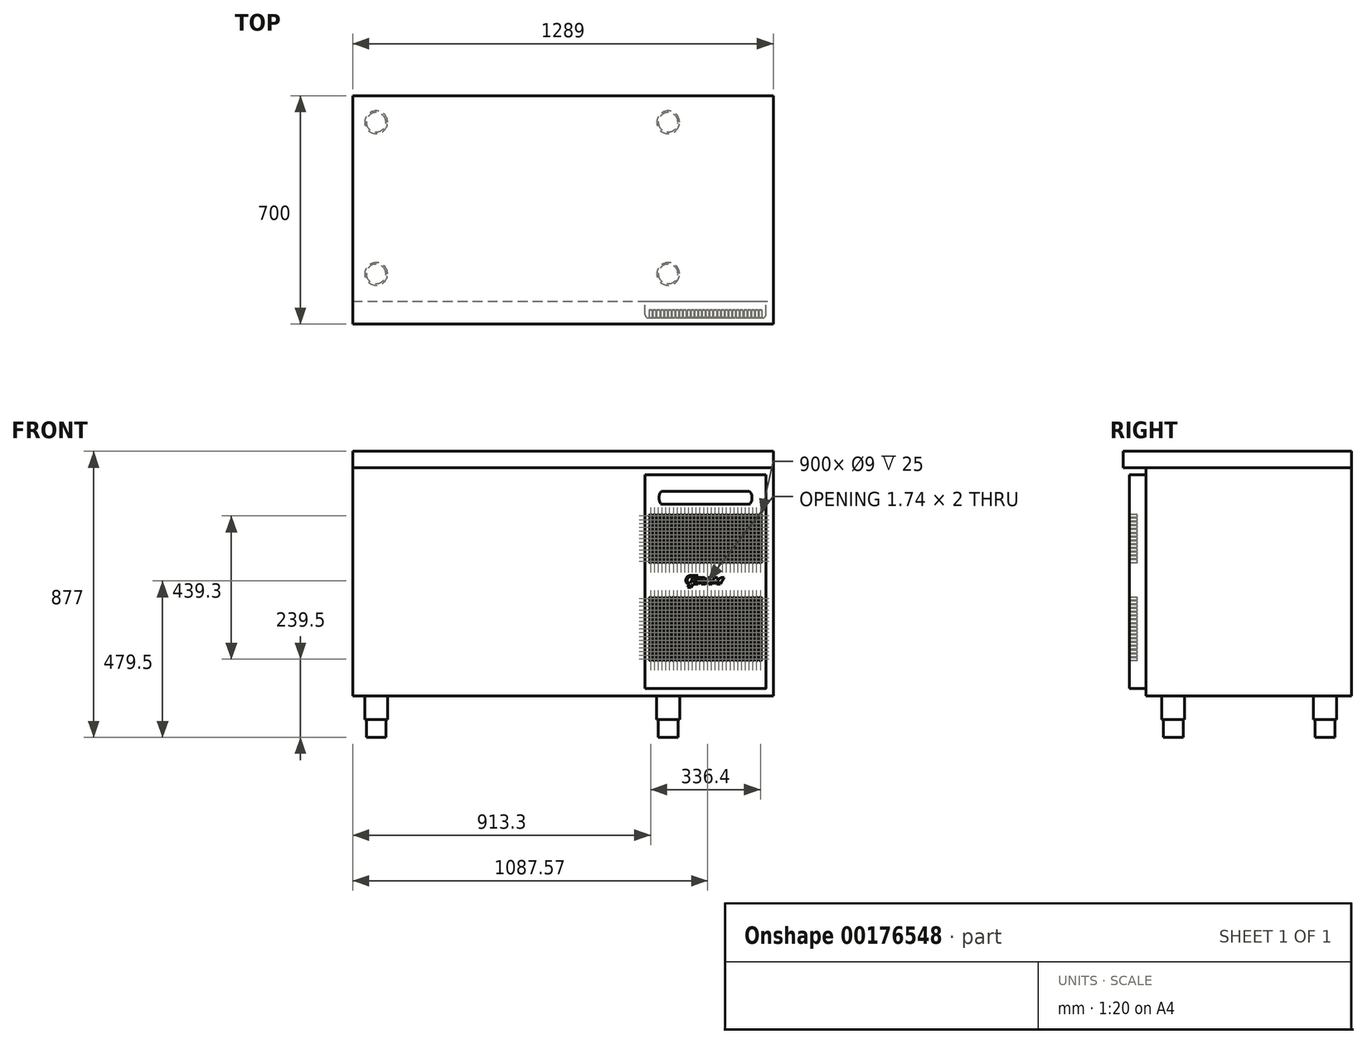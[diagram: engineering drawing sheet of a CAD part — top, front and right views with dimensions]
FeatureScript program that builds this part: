
annotation { "Feature Type Name" : "Feature", "Feature Type Description" : "" }
export const myFeature = defineFeature(function(context is Context, id is Id, definition is map)
    precondition{}
    {
        {
            var Q0;
            Q0=qCreatedBy(makeId("Top.planeOp"),FACE);
            var sketch = newSketch(context, id + "F0", { "sketchPlane" : qUnion([Q0])});
            skLineSegment(sketch, "E0.bottom", {"start": v(644.5, 350) * mm, "end": v(-644.5, 350) * mm});
            skLineSegment(sketch, "E0.top", {"start": v(644.5, -350) * mm, "end": v(-644.5, -350) * mm});
            skLineSegment(sketch, "E0.left", {"start": v(644.5, 350) * mm, "end": v(644.5, -350) * mm});
            skLineSegment(sketch, "E0.right", {"start": v(-644.5, 350) * mm, "end": v(-644.5, -350) * mm});
            skPoint(sketch, "E0.middle", {"position": v(0, 0) * mm});
            skSolve(sketch);
        }
        {
            var Q0;
            Q0 = qSketchRegion(id + "F0", true);
            extrude(context, id + "F1", {"entities" : qUnion([Q0]), "depth" : 50 * mm});
        }
        {
            var Q0;
            Q0=makeQuery(id+"F1.opExtrude","CAP_FACE",FACE,{"disambiguationData":[OSD([sQuery(id+"F0.wireOp",EDGE,"E0.bottom"),sQuery(id+"F0.wireOp",EDGE,"E0.top"),sQuery(id+"F0.wireOp",EDGE,"E0.left"),sQuery(id+"F0.wireOp",EDGE,"E0.right")])],"isStart":true});
            var sketch = newSketch(context, id + "F2", { "sketchPlane" : qUnion([Q0])});
            skLineSegment(sketch, "E1.bottom", {"start": v(-644.5, -350) * mm, "end": v(644.5, -350) * mm});
            skLineSegment(sketch, "E1.top", {"start": v(-644.5, 280) * mm, "end": v(644.5, 280) * mm});
            skLineSegment(sketch, "E1.left", {"start": v(-644.5, -350) * mm, "end": v(-644.5, 280) * mm});
            skLineSegment(sketch, "E1.right", {"start": v(644.5, -350) * mm, "end": v(644.5, 280) * mm});
            skSolve(sketch);
        }
        {
            var Q0;
            Q0 = qSketchRegion(id + "F2", true);
            extrude(context, id + "F3", {"entities" : qUnion([Q0]), "depth" : 700 * mm});
        }
        {
            var Q0;
            Q0=makeQuery(id+"F3.opExtrude","CAP_FACE",FACE,{"disambiguationData":[OSD([sQuery(id+"F2.wireOp",EDGE,"E1.bottom"),sQuery(id+"F2.wireOp",EDGE,"E1.top"),sQuery(id+"F2.wireOp",EDGE,"E1.left"),sQuery(id+"F2.wireOp",EDGE,"E1.right")])],"isStart":false});
            var sketch = newSketch(context, id + "F4", { "sketchPlane" : qUnion([Q0])});
            skCircle(sketch, "E2", {"center": v(-572.5, 196) * mm, "radius": 35 * mm});
            skCircle(sketch, "E3", {"center": v(322.5, 196) * mm, "radius": 35 * mm});
            skCircle(sketch, "E4", {"center": v(322.5, -269) * mm, "radius": 35 * mm});
            skCircle(sketch, "E5", {"center": v(-572.5, -269) * mm, "radius": 35 * mm});
            skSolve(sketch);
        }
        {
            var Q0;
            Q0 = qSketchRegion(id + "F4", true);
            extrude(context, id + "F5", {"entities" : qUnion([Q0]), "operationType" : NewBodyOperationType.ADD, "offsetDistance" : 25 * mm, "depth" : 72 * mm});
        }
        {
            var Q0;
            Q0=makeQuery(id+"F5.opExtrude","CAP_FACE",FACE,{"disambiguationData":[OSD([sQuery(id+"F4.wireOp",EDGE,"E2")])],"isStart":false});
            var sketch = newSketch(context, id + "F6", { "sketchPlane" : qUnion([Q0])});
            skCircle(sketch, "E6", {"center": v(-572.5, 196) * mm, "radius": 30 * mm});
            skCircle(sketch, "E7", {"center": v(322.5, 196) * mm, "radius": 30 * mm});
            skCircle(sketch, "E8", {"center": v(322.5, -269) * mm, "radius": 30 * mm});
            skCircle(sketch, "E9", {"center": v(-572.5, -269) * mm, "radius": 30 * mm});
            skSolve(sketch);
        }
        {
            var Q0;
            Q0 = qSketchRegion(id + "F6", true);
            extrude(context, id + "F7", {"entities" : qUnion([Q0]), "operationType" : NewBodyOperationType.ADD, "depth" : 55 * mm});
        }
        {
            var Q0;
            Q0=makeQuery(id+"F3.opExtrude","SWEPT_FACE",FACE,{"disambiguationData":[OSD([sQuery(id+"F2.wireOp",EDGE,"E1.top")])]});
            var sketch = newSketch(context, id + "F8", { "sketchPlane" : qUnion([Q0])});
            skLineSegment(sketch, "E10.bottom", {"start": v(252, -22.5) * mm, "end": v(622, -22.5) * mm});
            skLineSegment(sketch, "E10.top", {"start": v(252, -677.5) * mm, "end": v(622, -677.5) * mm});
            skLineSegment(sketch, "E10.left", {"start": v(252, -22.5) * mm, "end": v(252, -677.5) * mm});
            skLineSegment(sketch, "E10.right", {"start": v(622, -22.5) * mm, "end": v(622, -677.5) * mm});
            skSolve(sketch);
        }
        {
            var Q0;
            Q0 = qSketchRegion(id + "F8", true);
            extrude(context, id + "F9", {"entities" : qUnion([Q0]), "operationType" : NewBodyOperationType.ADD, "depth" : 51 * mm});
        }
        {
            var Q0;
            Q0=makeQuery(id+"F9.opExtrude","CAP_EDGE",EDGE,{"disambiguationData":[OSD([sQuery(id+"F8.wireOp",EDGE,"E10.left")])],"isStart":false});
            var Q1;
            Q1=makeQuery(id+"F9.opExtrude","CAP_EDGE",EDGE,{"disambiguationData":[OSD([sQuery(id+"F8.wireOp",EDGE,"E10.right")])],"isStart":false});
            fillet(context, id + "F10", {"entities" : qUnion([Q0, Q1]), "radius" : 10 * mm, "tangentPropagation" : true, "allowEdgeOverflow" : false});
        }
        {
            var Q0;
            Q0=makeQuery(id+"F9.opExtrude","CAP_FACE",FACE,{"disambiguationData":[OSD([sQuery(id+"F8.wireOp",EDGE,"E10.bottom"),sQuery(id+"F8.wireOp",EDGE,"E10.top"),sQuery(id+"F8.wireOp",EDGE,"E10.left"),sQuery(id+"F8.wireOp",EDGE,"E10.right")])],"isStart":false});
            var sketch = newSketch(context, id + "F11", { "sketchPlane" : qUnion([Q0])});
            skCircle(sketch, "E11", {"center": v(268.8, -587.5) * mm, "radius": 4.5 * mm});
            skCircle(sketch, "E12.0.1.0", {"center": v(268.8, -575.9) * mm, "radius": 4.5 * mm});
            skCircle(sketch, "E12.0.2.0", {"center": v(268.8, -564.3) * mm, "radius": 4.5 * mm});
            skCircle(sketch, "E12.0.3.0", {"center": v(268.8, -552.7) * mm, "radius": 4.5 * mm});
            skCircle(sketch, "E12.0.4.0", {"center": v(268.8, -541.1) * mm, "radius": 4.5 * mm});
            skCircle(sketch, "E12.0.5.0", {"center": v(268.8, -529.5) * mm, "radius": 4.5 * mm});
            skCircle(sketch, "E12.0.6.0", {"center": v(268.8, -517.9) * mm, "radius": 4.5 * mm});
            skCircle(sketch, "E12.0.7.0", {"center": v(268.8, -506.3) * mm, "radius": 4.5 * mm});
            skCircle(sketch, "E12.0.8.0", {"center": v(268.8, -494.7) * mm, "radius": 4.5 * mm});
            skCircle(sketch, "E12.0.9.0", {"center": v(268.8, -483.1) * mm, "radius": 4.5 * mm});
            skCircle(sketch, "E12.0.10.0", {"center": v(268.8, -471.5) * mm, "radius": 4.5 * mm});
            skCircle(sketch, "E12.0.11.0", {"center": v(268.8, -459.9) * mm, "radius": 4.5 * mm});
            skCircle(sketch, "E12.0.12.0", {"center": v(268.8, -448.3) * mm, "radius": 4.5 * mm});
            skCircle(sketch, "E12.0.13.0", {"center": v(268.8, -436.7) * mm, "radius": 4.5 * mm});
            skCircle(sketch, "E12.0.14.0", {"center": v(268.8, -425.1) * mm, "radius": 4.5 * mm});
            skCircle(sketch, "E12.0.15.0", {"center": v(268.8, -413.5) * mm, "radius": 4.5 * mm});
            skCircle(sketch, "E12.0.16.0", {"center": v(268.8, -401.9) * mm, "radius": 4.5 * mm});
            skCircle(sketch, "E12.1.0.0", {"center": v(280.4, -587.5) * mm, "radius": 4.5 * mm});
            skCircle(sketch, "E12.1.1.0", {"center": v(280.4, -575.9) * mm, "radius": 4.5 * mm});
            skCircle(sketch, "E12.1.2.0", {"center": v(280.4, -564.3) * mm, "radius": 4.5 * mm});
            skCircle(sketch, "E12.1.3.0", {"center": v(280.4, -552.7) * mm, "radius": 4.5 * mm});
            skCircle(sketch, "E12.1.4.0", {"center": v(280.4, -541.1) * mm, "radius": 4.5 * mm});
            skCircle(sketch, "E12.1.5.0", {"center": v(280.4, -529.5) * mm, "radius": 4.5 * mm});
            skCircle(sketch, "E12.1.6.0", {"center": v(280.4, -517.9) * mm, "radius": 4.5 * mm});
            skCircle(sketch, "E12.1.7.0", {"center": v(280.4, -506.3) * mm, "radius": 4.5 * mm});
            skCircle(sketch, "E12.1.8.0", {"center": v(280.4, -494.7) * mm, "radius": 4.5 * mm});
            skCircle(sketch, "E12.1.9.0", {"center": v(280.4, -483.1) * mm, "radius": 4.5 * mm});
            skCircle(sketch, "E12.1.10.0", {"center": v(280.4, -471.5) * mm, "radius": 4.5 * mm});
            skCircle(sketch, "E12.1.11.0", {"center": v(280.4, -459.9) * mm, "radius": 4.5 * mm});
            skCircle(sketch, "E12.1.12.0", {"center": v(280.4, -448.3) * mm, "radius": 4.5 * mm});
            skCircle(sketch, "E12.1.13.0", {"center": v(280.4, -436.7) * mm, "radius": 4.5 * mm});
            skCircle(sketch, "E12.1.14.0", {"center": v(280.4, -425.1) * mm, "radius": 4.5 * mm});
            skCircle(sketch, "E12.1.15.0", {"center": v(280.4, -413.5) * mm, "radius": 4.5 * mm});
            skCircle(sketch, "E12.1.16.0", {"center": v(280.4, -401.9) * mm, "radius": 4.5 * mm});
            skCircle(sketch, "E12.2.0.0", {"center": v(292, -587.5) * mm, "radius": 4.5 * mm});
            skCircle(sketch, "E12.2.1.0", {"center": v(292, -575.9) * mm, "radius": 4.5 * mm});
            skCircle(sketch, "E12.2.2.0", {"center": v(292, -564.3) * mm, "radius": 4.5 * mm});
            skCircle(sketch, "E12.2.3.0", {"center": v(292, -552.7) * mm, "radius": 4.5 * mm});
            skCircle(sketch, "E12.2.4.0", {"center": v(292, -541.1) * mm, "radius": 4.5 * mm});
            skCircle(sketch, "E12.2.5.0", {"center": v(292, -529.5) * mm, "radius": 4.5 * mm});
            skCircle(sketch, "E12.2.6.0", {"center": v(292, -517.9) * mm, "radius": 4.5 * mm});
            skCircle(sketch, "E12.2.7.0", {"center": v(292, -506.3) * mm, "radius": 4.5 * mm});
            skCircle(sketch, "E12.2.8.0", {"center": v(292, -494.7) * mm, "radius": 4.5 * mm});
            skCircle(sketch, "E12.2.9.0", {"center": v(292, -483.1) * mm, "radius": 4.5 * mm});
            skCircle(sketch, "E12.2.10.0", {"center": v(292, -471.5) * mm, "radius": 4.5 * mm});
            skCircle(sketch, "E12.2.11.0", {"center": v(292, -459.9) * mm, "radius": 4.5 * mm});
            skCircle(sketch, "E12.2.12.0", {"center": v(292, -448.3) * mm, "radius": 4.5 * mm});
            skCircle(sketch, "E12.2.13.0", {"center": v(292, -436.7) * mm, "radius": 4.5 * mm});
            skCircle(sketch, "E12.2.14.0", {"center": v(292, -425.1) * mm, "radius": 4.5 * mm});
            skCircle(sketch, "E12.2.15.0", {"center": v(292, -413.5) * mm, "radius": 4.5 * mm});
            skCircle(sketch, "E12.2.16.0", {"center": v(292, -401.9) * mm, "radius": 4.5 * mm});
            skCircle(sketch, "E12.3.0.0", {"center": v(303.6, -587.5) * mm, "radius": 4.5 * mm});
            skCircle(sketch, "E12.3.1.0", {"center": v(303.6, -575.9) * mm, "radius": 4.5 * mm});
            skCircle(sketch, "E12.3.2.0", {"center": v(303.6, -564.3) * mm, "radius": 4.5 * mm});
            skCircle(sketch, "E12.3.3.0", {"center": v(303.6, -552.7) * mm, "radius": 4.5 * mm});
            skCircle(sketch, "E12.3.4.0", {"center": v(303.6, -541.1) * mm, "radius": 4.5 * mm});
            skCircle(sketch, "E12.3.5.0", {"center": v(303.6, -529.5) * mm, "radius": 4.5 * mm});
            skCircle(sketch, "E12.3.6.0", {"center": v(303.6, -517.9) * mm, "radius": 4.5 * mm});
            skCircle(sketch, "E12.3.7.0", {"center": v(303.6, -506.3) * mm, "radius": 4.5 * mm});
            skCircle(sketch, "E12.3.8.0", {"center": v(303.6, -494.7) * mm, "radius": 4.5 * mm});
            skCircle(sketch, "E12.3.9.0", {"center": v(303.6, -483.1) * mm, "radius": 4.5 * mm});
            skCircle(sketch, "E12.3.10.0", {"center": v(303.6, -471.5) * mm, "radius": 4.5 * mm});
            skCircle(sketch, "E12.3.11.0", {"center": v(303.6, -459.9) * mm, "radius": 4.5 * mm});
            skCircle(sketch, "E12.3.12.0", {"center": v(303.6, -448.3) * mm, "radius": 4.5 * mm});
            skCircle(sketch, "E12.3.13.0", {"center": v(303.6, -436.7) * mm, "radius": 4.5 * mm});
            skCircle(sketch, "E12.3.14.0", {"center": v(303.6, -425.1) * mm, "radius": 4.5 * mm});
            skCircle(sketch, "E12.3.15.0", {"center": v(303.6, -413.5) * mm, "radius": 4.5 * mm});
            skCircle(sketch, "E12.3.16.0", {"center": v(303.6, -401.9) * mm, "radius": 4.5 * mm});
            skCircle(sketch, "E12.4.0.0", {"center": v(315.2, -587.5) * mm, "radius": 4.5 * mm});
            skCircle(sketch, "E12.4.1.0", {"center": v(315.2, -575.9) * mm, "radius": 4.5 * mm});
            skCircle(sketch, "E12.4.2.0", {"center": v(315.2, -564.3) * mm, "radius": 4.5 * mm});
            skCircle(sketch, "E12.4.3.0", {"center": v(315.2, -552.7) * mm, "radius": 4.5 * mm});
            skCircle(sketch, "E12.4.4.0", {"center": v(315.2, -541.1) * mm, "radius": 4.5 * mm});
            skCircle(sketch, "E12.4.5.0", {"center": v(315.2, -529.5) * mm, "radius": 4.5 * mm});
            skCircle(sketch, "E12.4.6.0", {"center": v(315.2, -517.9) * mm, "radius": 4.5 * mm});
            skCircle(sketch, "E12.4.7.0", {"center": v(315.2, -506.3) * mm, "radius": 4.5 * mm});
            skCircle(sketch, "E12.4.8.0", {"center": v(315.2, -494.7) * mm, "radius": 4.5 * mm});
            skCircle(sketch, "E12.4.9.0", {"center": v(315.2, -483.1) * mm, "radius": 4.5 * mm});
            skCircle(sketch, "E12.4.10.0", {"center": v(315.2, -471.5) * mm, "radius": 4.5 * mm});
            skCircle(sketch, "E12.4.11.0", {"center": v(315.2, -459.9) * mm, "radius": 4.5 * mm});
            skCircle(sketch, "E12.4.12.0", {"center": v(315.2, -448.3) * mm, "radius": 4.5 * mm});
            skCircle(sketch, "E12.4.13.0", {"center": v(315.2, -436.7) * mm, "radius": 4.5 * mm});
            skCircle(sketch, "E12.4.14.0", {"center": v(315.2, -425.1) * mm, "radius": 4.5 * mm});
            skCircle(sketch, "E12.4.15.0", {"center": v(315.2, -413.5) * mm, "radius": 4.5 * mm});
            skCircle(sketch, "E12.4.16.0", {"center": v(315.2, -401.9) * mm, "radius": 4.5 * mm});
            skCircle(sketch, "E12.5.0.0", {"center": v(326.8, -587.5) * mm, "radius": 4.5 * mm});
            skCircle(sketch, "E12.5.1.0", {"center": v(326.8, -575.9) * mm, "radius": 4.5 * mm});
            skCircle(sketch, "E12.5.2.0", {"center": v(326.8, -564.3) * mm, "radius": 4.5 * mm});
            skCircle(sketch, "E12.5.3.0", {"center": v(326.8, -552.7) * mm, "radius": 4.5 * mm});
            skCircle(sketch, "E12.5.4.0", {"center": v(326.8, -541.1) * mm, "radius": 4.5 * mm});
            skCircle(sketch, "E12.5.5.0", {"center": v(326.8, -529.5) * mm, "radius": 4.5 * mm});
            skCircle(sketch, "E12.5.6.0", {"center": v(326.8, -517.9) * mm, "radius": 4.5 * mm});
            skCircle(sketch, "E12.5.7.0", {"center": v(326.8, -506.3) * mm, "radius": 4.5 * mm});
            skCircle(sketch, "E12.5.8.0", {"center": v(326.8, -494.7) * mm, "radius": 4.5 * mm});
            skCircle(sketch, "E12.5.9.0", {"center": v(326.8, -483.1) * mm, "radius": 4.5 * mm});
            skCircle(sketch, "E12.5.10.0", {"center": v(326.8, -471.5) * mm, "radius": 4.5 * mm});
            skCircle(sketch, "E12.5.11.0", {"center": v(326.8, -459.9) * mm, "radius": 4.5 * mm});
            skCircle(sketch, "E12.5.12.0", {"center": v(326.8, -448.3) * mm, "radius": 4.5 * mm});
            skCircle(sketch, "E12.5.13.0", {"center": v(326.8, -436.7) * mm, "radius": 4.5 * mm});
            skCircle(sketch, "E12.5.14.0", {"center": v(326.8, -425.1) * mm, "radius": 4.5 * mm});
            skCircle(sketch, "E12.5.15.0", {"center": v(326.8, -413.5) * mm, "radius": 4.5 * mm});
            skCircle(sketch, "E12.5.16.0", {"center": v(326.8, -401.9) * mm, "radius": 4.5 * mm});
            skCircle(sketch, "E12.6.0.0", {"center": v(338.4, -587.5) * mm, "radius": 4.5 * mm});
            skCircle(sketch, "E12.6.1.0", {"center": v(338.4, -575.9) * mm, "radius": 4.5 * mm});
            skCircle(sketch, "E12.6.2.0", {"center": v(338.4, -564.3) * mm, "radius": 4.5 * mm});
            skCircle(sketch, "E12.6.3.0", {"center": v(338.4, -552.7) * mm, "radius": 4.5 * mm});
            skCircle(sketch, "E12.6.4.0", {"center": v(338.4, -541.1) * mm, "radius": 4.5 * mm});
            skCircle(sketch, "E12.6.5.0", {"center": v(338.4, -529.5) * mm, "radius": 4.5 * mm});
            skCircle(sketch, "E12.6.6.0", {"center": v(338.4, -517.9) * mm, "radius": 4.5 * mm});
            skCircle(sketch, "E12.6.7.0", {"center": v(338.4, -506.3) * mm, "radius": 4.5 * mm});
            skCircle(sketch, "E12.6.8.0", {"center": v(338.4, -494.7) * mm, "radius": 4.5 * mm});
            skCircle(sketch, "E12.6.9.0", {"center": v(338.4, -483.1) * mm, "radius": 4.5 * mm});
            skCircle(sketch, "E12.6.10.0", {"center": v(338.4, -471.5) * mm, "radius": 4.5 * mm});
            skCircle(sketch, "E12.6.11.0", {"center": v(338.4, -459.9) * mm, "radius": 4.5 * mm});
            skCircle(sketch, "E12.6.12.0", {"center": v(338.4, -448.3) * mm, "radius": 4.5 * mm});
            skCircle(sketch, "E12.6.13.0", {"center": v(338.4, -436.7) * mm, "radius": 4.5 * mm});
            skCircle(sketch, "E12.6.14.0", {"center": v(338.4, -425.1) * mm, "radius": 4.5 * mm});
            skCircle(sketch, "E12.6.15.0", {"center": v(338.4, -413.5) * mm, "radius": 4.5 * mm});
            skCircle(sketch, "E12.6.16.0", {"center": v(338.4, -401.9) * mm, "radius": 4.5 * mm});
            skCircle(sketch, "E12.7.0.0", {"center": v(350, -587.5) * mm, "radius": 4.5 * mm});
            skCircle(sketch, "E12.7.1.0", {"center": v(350, -575.9) * mm, "radius": 4.5 * mm});
            skCircle(sketch, "E12.7.2.0", {"center": v(350, -564.3) * mm, "radius": 4.5 * mm});
            skCircle(sketch, "E12.7.3.0", {"center": v(350, -552.7) * mm, "radius": 4.5 * mm});
            skCircle(sketch, "E12.7.4.0", {"center": v(350, -541.1) * mm, "radius": 4.5 * mm});
            skCircle(sketch, "E12.7.5.0", {"center": v(350, -529.5) * mm, "radius": 4.5 * mm});
            skCircle(sketch, "E12.7.6.0", {"center": v(350, -517.9) * mm, "radius": 4.5 * mm});
            skCircle(sketch, "E12.7.7.0", {"center": v(350, -506.3) * mm, "radius": 4.5 * mm});
            skCircle(sketch, "E12.7.8.0", {"center": v(350, -494.7) * mm, "radius": 4.5 * mm});
            skCircle(sketch, "E12.7.9.0", {"center": v(350, -483.1) * mm, "radius": 4.5 * mm});
            skCircle(sketch, "E12.7.10.0", {"center": v(350, -471.5) * mm, "radius": 4.5 * mm});
            skCircle(sketch, "E12.7.11.0", {"center": v(350, -459.9) * mm, "radius": 4.5 * mm});
            skCircle(sketch, "E12.7.12.0", {"center": v(350, -448.3) * mm, "radius": 4.5 * mm});
            skCircle(sketch, "E12.7.13.0", {"center": v(350, -436.7) * mm, "radius": 4.5 * mm});
            skCircle(sketch, "E12.7.14.0", {"center": v(350, -425.1) * mm, "radius": 4.5 * mm});
            skCircle(sketch, "E12.7.15.0", {"center": v(350, -413.5) * mm, "radius": 4.5 * mm});
            skCircle(sketch, "E12.7.16.0", {"center": v(350, -401.9) * mm, "radius": 4.5 * mm});
            skCircle(sketch, "E12.8.0.0", {"center": v(361.6, -587.5) * mm, "radius": 4.5 * mm});
            skCircle(sketch, "E12.8.1.0", {"center": v(361.6, -575.9) * mm, "radius": 4.5 * mm});
            skCircle(sketch, "E12.8.2.0", {"center": v(361.6, -564.3) * mm, "radius": 4.5 * mm});
            skCircle(sketch, "E12.8.3.0", {"center": v(361.6, -552.7) * mm, "radius": 4.5 * mm});
            skCircle(sketch, "E12.8.4.0", {"center": v(361.6, -541.1) * mm, "radius": 4.5 * mm});
            skCircle(sketch, "E12.8.5.0", {"center": v(361.6, -529.5) * mm, "radius": 4.5 * mm});
            skCircle(sketch, "E12.8.6.0", {"center": v(361.6, -517.9) * mm, "radius": 4.5 * mm});
            skCircle(sketch, "E12.8.7.0", {"center": v(361.6, -506.3) * mm, "radius": 4.5 * mm});
            skCircle(sketch, "E12.8.8.0", {"center": v(361.6, -494.7) * mm, "radius": 4.5 * mm});
            skCircle(sketch, "E12.8.9.0", {"center": v(361.6, -483.1) * mm, "radius": 4.5 * mm});
            skCircle(sketch, "E12.8.10.0", {"center": v(361.6, -471.5) * mm, "radius": 4.5 * mm});
            skCircle(sketch, "E12.8.11.0", {"center": v(361.6, -459.9) * mm, "radius": 4.5 * mm});
            skCircle(sketch, "E12.8.12.0", {"center": v(361.6, -448.3) * mm, "radius": 4.5 * mm});
            skCircle(sketch, "E12.8.13.0", {"center": v(361.6, -436.7) * mm, "radius": 4.5 * mm});
            skCircle(sketch, "E12.8.14.0", {"center": v(361.6, -425.1) * mm, "radius": 4.5 * mm});
            skCircle(sketch, "E12.8.15.0", {"center": v(361.6, -413.5) * mm, "radius": 4.5 * mm});
            skCircle(sketch, "E12.8.16.0", {"center": v(361.6, -401.9) * mm, "radius": 4.5 * mm});
            skCircle(sketch, "E12.9.0.0", {"center": v(373.2, -587.5) * mm, "radius": 4.5 * mm});
            skCircle(sketch, "E12.9.1.0", {"center": v(373.2, -575.9) * mm, "radius": 4.5 * mm});
            skCircle(sketch, "E12.9.2.0", {"center": v(373.2, -564.3) * mm, "radius": 4.5 * mm});
            skCircle(sketch, "E12.9.3.0", {"center": v(373.2, -552.7) * mm, "radius": 4.5 * mm});
            skCircle(sketch, "E12.9.4.0", {"center": v(373.2, -541.1) * mm, "radius": 4.5 * mm});
            skCircle(sketch, "E12.9.5.0", {"center": v(373.2, -529.5) * mm, "radius": 4.5 * mm});
            skCircle(sketch, "E12.9.6.0", {"center": v(373.2, -517.9) * mm, "radius": 4.5 * mm});
            skCircle(sketch, "E12.9.7.0", {"center": v(373.2, -506.3) * mm, "radius": 4.5 * mm});
            skCircle(sketch, "E12.9.8.0", {"center": v(373.2, -494.7) * mm, "radius": 4.5 * mm});
            skCircle(sketch, "E12.9.9.0", {"center": v(373.2, -483.1) * mm, "radius": 4.5 * mm});
            skCircle(sketch, "E12.9.10.0", {"center": v(373.2, -471.5) * mm, "radius": 4.5 * mm});
            skCircle(sketch, "E12.9.11.0", {"center": v(373.2, -459.9) * mm, "radius": 4.5 * mm});
            skCircle(sketch, "E12.9.12.0", {"center": v(373.2, -448.3) * mm, "radius": 4.5 * mm});
            skCircle(sketch, "E12.9.13.0", {"center": v(373.2, -436.7) * mm, "radius": 4.5 * mm});
            skCircle(sketch, "E12.9.14.0", {"center": v(373.2, -425.1) * mm, "radius": 4.5 * mm});
            skCircle(sketch, "E12.9.15.0", {"center": v(373.2, -413.5) * mm, "radius": 4.5 * mm});
            skCircle(sketch, "E12.9.16.0", {"center": v(373.2, -401.9) * mm, "radius": 4.5 * mm});
            skCircle(sketch, "E12.10.0.0", {"center": v(384.8, -587.5) * mm, "radius": 4.5 * mm});
            skCircle(sketch, "E12.10.1.0", {"center": v(384.8, -575.9) * mm, "radius": 4.5 * mm});
            skCircle(sketch, "E12.10.2.0", {"center": v(384.8, -564.3) * mm, "radius": 4.5 * mm});
            skCircle(sketch, "E12.10.3.0", {"center": v(384.8, -552.7) * mm, "radius": 4.5 * mm});
            skCircle(sketch, "E12.10.4.0", {"center": v(384.8, -541.1) * mm, "radius": 4.5 * mm});
            skCircle(sketch, "E12.10.5.0", {"center": v(384.8, -529.5) * mm, "radius": 4.5 * mm});
            skCircle(sketch, "E12.10.6.0", {"center": v(384.8, -517.9) * mm, "radius": 4.5 * mm});
            skCircle(sketch, "E12.10.7.0", {"center": v(384.8, -506.3) * mm, "radius": 4.5 * mm});
            skCircle(sketch, "E12.10.8.0", {"center": v(384.8, -494.7) * mm, "radius": 4.5 * mm});
            skCircle(sketch, "E12.10.9.0", {"center": v(384.8, -483.1) * mm, "radius": 4.5 * mm});
            skCircle(sketch, "E12.10.10.0", {"center": v(384.8, -471.5) * mm, "radius": 4.5 * mm});
            skCircle(sketch, "E12.10.11.0", {"center": v(384.8, -459.9) * mm, "radius": 4.5 * mm});
            skCircle(sketch, "E12.10.12.0", {"center": v(384.8, -448.3) * mm, "radius": 4.5 * mm});
            skCircle(sketch, "E12.10.13.0", {"center": v(384.8, -436.7) * mm, "radius": 4.5 * mm});
            skCircle(sketch, "E12.10.14.0", {"center": v(384.8, -425.1) * mm, "radius": 4.5 * mm});
            skCircle(sketch, "E12.10.15.0", {"center": v(384.8, -413.5) * mm, "radius": 4.5 * mm});
            skCircle(sketch, "E12.10.16.0", {"center": v(384.8, -401.9) * mm, "radius": 4.5 * mm});
            skCircle(sketch, "E12.11.0.0", {"center": v(396.4, -587.5) * mm, "radius": 4.5 * mm});
            skCircle(sketch, "E12.11.1.0", {"center": v(396.4, -575.9) * mm, "radius": 4.5 * mm});
            skCircle(sketch, "E12.11.2.0", {"center": v(396.4, -564.3) * mm, "radius": 4.5 * mm});
            skCircle(sketch, "E12.11.3.0", {"center": v(396.4, -552.7) * mm, "radius": 4.5 * mm});
            skCircle(sketch, "E12.11.4.0", {"center": v(396.4, -541.1) * mm, "radius": 4.5 * mm});
            skCircle(sketch, "E12.11.5.0", {"center": v(396.4, -529.5) * mm, "radius": 4.5 * mm});
            skCircle(sketch, "E12.11.6.0", {"center": v(396.4, -517.9) * mm, "radius": 4.5 * mm});
            skCircle(sketch, "E12.11.7.0", {"center": v(396.4, -506.3) * mm, "radius": 4.5 * mm});
            skCircle(sketch, "E12.11.8.0", {"center": v(396.4, -494.7) * mm, "radius": 4.5 * mm});
            skCircle(sketch, "E12.11.9.0", {"center": v(396.4, -483.1) * mm, "radius": 4.5 * mm});
            skCircle(sketch, "E12.11.10.0", {"center": v(396.4, -471.5) * mm, "radius": 4.5 * mm});
            skCircle(sketch, "E12.11.11.0", {"center": v(396.4, -459.9) * mm, "radius": 4.5 * mm});
            skCircle(sketch, "E12.11.12.0", {"center": v(396.4, -448.3) * mm, "radius": 4.5 * mm});
            skCircle(sketch, "E12.11.13.0", {"center": v(396.4, -436.7) * mm, "radius": 4.5 * mm});
            skCircle(sketch, "E12.11.14.0", {"center": v(396.4, -425.1) * mm, "radius": 4.5 * mm});
            skCircle(sketch, "E12.11.15.0", {"center": v(396.4, -413.5) * mm, "radius": 4.5 * mm});
            skCircle(sketch, "E12.11.16.0", {"center": v(396.4, -401.9) * mm, "radius": 4.5 * mm});
            skCircle(sketch, "E12.12.0.0", {"center": v(408, -587.5) * mm, "radius": 4.5 * mm});
            skCircle(sketch, "E12.12.1.0", {"center": v(408, -575.9) * mm, "radius": 4.5 * mm});
            skCircle(sketch, "E12.12.2.0", {"center": v(408, -564.3) * mm, "radius": 4.5 * mm});
            skCircle(sketch, "E12.12.3.0", {"center": v(408, -552.7) * mm, "radius": 4.5 * mm});
            skCircle(sketch, "E12.12.4.0", {"center": v(408, -541.1) * mm, "radius": 4.5 * mm});
            skCircle(sketch, "E12.12.5.0", {"center": v(408, -529.5) * mm, "radius": 4.5 * mm});
            skCircle(sketch, "E12.12.6.0", {"center": v(408, -517.9) * mm, "radius": 4.5 * mm});
            skCircle(sketch, "E12.12.7.0", {"center": v(408, -506.3) * mm, "radius": 4.5 * mm});
            skCircle(sketch, "E12.12.8.0", {"center": v(408, -494.7) * mm, "radius": 4.5 * mm});
            skCircle(sketch, "E12.12.9.0", {"center": v(408, -483.1) * mm, "radius": 4.5 * mm});
            skCircle(sketch, "E12.12.10.0", {"center": v(408, -471.5) * mm, "radius": 4.5 * mm});
            skCircle(sketch, "E12.12.11.0", {"center": v(408, -459.9) * mm, "radius": 4.5 * mm});
            skCircle(sketch, "E12.12.12.0", {"center": v(408, -448.3) * mm, "radius": 4.5 * mm});
            skCircle(sketch, "E12.12.13.0", {"center": v(408, -436.7) * mm, "radius": 4.5 * mm});
            skCircle(sketch, "E12.12.14.0", {"center": v(408, -425.1) * mm, "radius": 4.5 * mm});
            skCircle(sketch, "E12.12.15.0", {"center": v(408, -413.5) * mm, "radius": 4.5 * mm});
            skCircle(sketch, "E12.12.16.0", {"center": v(408, -401.9) * mm, "radius": 4.5 * mm});
            skCircle(sketch, "E12.13.0.0", {"center": v(419.6, -587.5) * mm, "radius": 4.5 * mm});
            skCircle(sketch, "E12.13.1.0", {"center": v(419.6, -575.9) * mm, "radius": 4.5 * mm});
            skCircle(sketch, "E12.13.2.0", {"center": v(419.6, -564.3) * mm, "radius": 4.5 * mm});
            skCircle(sketch, "E12.13.3.0", {"center": v(419.6, -552.7) * mm, "radius": 4.5 * mm});
            skCircle(sketch, "E12.13.4.0", {"center": v(419.6, -541.1) * mm, "radius": 4.5 * mm});
            skCircle(sketch, "E12.13.5.0", {"center": v(419.6, -529.5) * mm, "radius": 4.5 * mm});
            skCircle(sketch, "E12.13.6.0", {"center": v(419.6, -517.9) * mm, "radius": 4.5 * mm});
            skCircle(sketch, "E12.13.7.0", {"center": v(419.6, -506.3) * mm, "radius": 4.5 * mm});
            skCircle(sketch, "E12.13.8.0", {"center": v(419.6, -494.7) * mm, "radius": 4.5 * mm});
            skCircle(sketch, "E12.13.9.0", {"center": v(419.6, -483.1) * mm, "radius": 4.5 * mm});
            skCircle(sketch, "E12.13.10.0", {"center": v(419.6, -471.5) * mm, "radius": 4.5 * mm});
            skCircle(sketch, "E12.13.11.0", {"center": v(419.6, -459.9) * mm, "radius": 4.5 * mm});
            skCircle(sketch, "E12.13.12.0", {"center": v(419.6, -448.3) * mm, "radius": 4.5 * mm});
            skCircle(sketch, "E12.13.13.0", {"center": v(419.6, -436.7) * mm, "radius": 4.5 * mm});
            skCircle(sketch, "E12.13.14.0", {"center": v(419.6, -425.1) * mm, "radius": 4.5 * mm});
            skCircle(sketch, "E12.13.15.0", {"center": v(419.6, -413.5) * mm, "radius": 4.5 * mm});
            skCircle(sketch, "E12.13.16.0", {"center": v(419.6, -401.9) * mm, "radius": 4.5 * mm});
            skCircle(sketch, "E12.14.0.0", {"center": v(431.2, -587.5) * mm, "radius": 4.5 * mm});
            skCircle(sketch, "E12.14.1.0", {"center": v(431.2, -575.9) * mm, "radius": 4.5 * mm});
            skCircle(sketch, "E12.14.2.0", {"center": v(431.2, -564.3) * mm, "radius": 4.5 * mm});
            skCircle(sketch, "E12.14.3.0", {"center": v(431.2, -552.7) * mm, "radius": 4.5 * mm});
            skCircle(sketch, "E12.14.4.0", {"center": v(431.2, -541.1) * mm, "radius": 4.5 * mm});
            skCircle(sketch, "E12.14.5.0", {"center": v(431.2, -529.5) * mm, "radius": 4.5 * mm});
            skCircle(sketch, "E12.14.6.0", {"center": v(431.2, -517.9) * mm, "radius": 4.5 * mm});
            skCircle(sketch, "E12.14.7.0", {"center": v(431.2, -506.3) * mm, "radius": 4.5 * mm});
            skCircle(sketch, "E12.14.8.0", {"center": v(431.2, -494.7) * mm, "radius": 4.5 * mm});
            skCircle(sketch, "E12.14.9.0", {"center": v(431.2, -483.1) * mm, "radius": 4.5 * mm});
            skCircle(sketch, "E12.14.10.0", {"center": v(431.2, -471.5) * mm, "radius": 4.5 * mm});
            skCircle(sketch, "E12.14.11.0", {"center": v(431.2, -459.9) * mm, "radius": 4.5 * mm});
            skCircle(sketch, "E12.14.12.0", {"center": v(431.2, -448.3) * mm, "radius": 4.5 * mm});
            skCircle(sketch, "E12.14.13.0", {"center": v(431.2, -436.7) * mm, "radius": 4.5 * mm});
            skCircle(sketch, "E12.14.14.0", {"center": v(431.2, -425.1) * mm, "radius": 4.5 * mm});
            skCircle(sketch, "E12.14.15.0", {"center": v(431.2, -413.5) * mm, "radius": 4.5 * mm});
            skCircle(sketch, "E12.14.16.0", {"center": v(431.2, -401.9) * mm, "radius": 4.5 * mm});
            skCircle(sketch, "E12.15.0.0", {"center": v(442.8, -587.5) * mm, "radius": 4.5 * mm});
            skCircle(sketch, "E12.15.1.0", {"center": v(442.8, -575.9) * mm, "radius": 4.5 * mm});
            skCircle(sketch, "E12.15.2.0", {"center": v(442.8, -564.3) * mm, "radius": 4.5 * mm});
            skCircle(sketch, "E12.15.3.0", {"center": v(442.8, -552.7) * mm, "radius": 4.5 * mm});
            skCircle(sketch, "E12.15.4.0", {"center": v(442.8, -541.1) * mm, "radius": 4.5 * mm});
            skCircle(sketch, "E12.15.5.0", {"center": v(442.8, -529.5) * mm, "radius": 4.5 * mm});
            skCircle(sketch, "E12.15.6.0", {"center": v(442.8, -517.9) * mm, "radius": 4.5 * mm});
            skCircle(sketch, "E12.15.7.0", {"center": v(442.8, -506.3) * mm, "radius": 4.5 * mm});
            skCircle(sketch, "E12.15.8.0", {"center": v(442.8, -494.7) * mm, "radius": 4.5 * mm});
            skCircle(sketch, "E12.15.9.0", {"center": v(442.8, -483.1) * mm, "radius": 4.5 * mm});
            skCircle(sketch, "E12.15.10.0", {"center": v(442.8, -471.5) * mm, "radius": 4.5 * mm});
            skCircle(sketch, "E12.15.11.0", {"center": v(442.8, -459.9) * mm, "radius": 4.5 * mm});
            skCircle(sketch, "E12.15.12.0", {"center": v(442.8, -448.3) * mm, "radius": 4.5 * mm});
            skCircle(sketch, "E12.15.13.0", {"center": v(442.8, -436.7) * mm, "radius": 4.5 * mm});
            skCircle(sketch, "E12.15.14.0", {"center": v(442.8, -425.1) * mm, "radius": 4.5 * mm});
            skCircle(sketch, "E12.15.15.0", {"center": v(442.8, -413.5) * mm, "radius": 4.5 * mm});
            skCircle(sketch, "E12.15.16.0", {"center": v(442.8, -401.9) * mm, "radius": 4.5 * mm});
            skCircle(sketch, "E12.16.0.0", {"center": v(454.4, -587.5) * mm, "radius": 4.5 * mm});
            skCircle(sketch, "E12.16.1.0", {"center": v(454.4, -575.9) * mm, "radius": 4.5 * mm});
            skCircle(sketch, "E12.16.2.0", {"center": v(454.4, -564.3) * mm, "radius": 4.5 * mm});
            skCircle(sketch, "E12.16.3.0", {"center": v(454.4, -552.7) * mm, "radius": 4.5 * mm});
            skCircle(sketch, "E12.16.4.0", {"center": v(454.4, -541.1) * mm, "radius": 4.5 * mm});
            skCircle(sketch, "E12.16.5.0", {"center": v(454.4, -529.5) * mm, "radius": 4.5 * mm});
            skCircle(sketch, "E12.16.6.0", {"center": v(454.4, -517.9) * mm, "radius": 4.5 * mm});
            skCircle(sketch, "E12.16.7.0", {"center": v(454.4, -506.3) * mm, "radius": 4.5 * mm});
            skCircle(sketch, "E12.16.8.0", {"center": v(454.4, -494.7) * mm, "radius": 4.5 * mm});
            skCircle(sketch, "E12.16.9.0", {"center": v(454.4, -483.1) * mm, "radius": 4.5 * mm});
            skCircle(sketch, "E12.16.10.0", {"center": v(454.4, -471.5) * mm, "radius": 4.5 * mm});
            skCircle(sketch, "E12.16.11.0", {"center": v(454.4, -459.9) * mm, "radius": 4.5 * mm});
            skCircle(sketch, "E12.16.12.0", {"center": v(454.4, -448.3) * mm, "radius": 4.5 * mm});
            skCircle(sketch, "E12.16.13.0", {"center": v(454.4, -436.7) * mm, "radius": 4.5 * mm});
            skCircle(sketch, "E12.16.14.0", {"center": v(454.4, -425.1) * mm, "radius": 4.5 * mm});
            skCircle(sketch, "E12.16.15.0", {"center": v(454.4, -413.5) * mm, "radius": 4.5 * mm});
            skCircle(sketch, "E12.16.16.0", {"center": v(454.4, -401.9) * mm, "radius": 4.5 * mm});
            skCircle(sketch, "E12.17.0.0", {"center": v(466, -587.5) * mm, "radius": 4.5 * mm});
            skCircle(sketch, "E12.17.1.0", {"center": v(466, -575.9) * mm, "radius": 4.5 * mm});
            skCircle(sketch, "E12.17.2.0", {"center": v(466, -564.3) * mm, "radius": 4.5 * mm});
            skCircle(sketch, "E12.17.3.0", {"center": v(466, -552.7) * mm, "radius": 4.5 * mm});
            skCircle(sketch, "E12.17.4.0", {"center": v(466, -541.1) * mm, "radius": 4.5 * mm});
            skCircle(sketch, "E12.17.5.0", {"center": v(466, -529.5) * mm, "radius": 4.5 * mm});
            skCircle(sketch, "E12.17.6.0", {"center": v(466, -517.9) * mm, "radius": 4.5 * mm});
            skCircle(sketch, "E12.17.7.0", {"center": v(466, -506.3) * mm, "radius": 4.5 * mm});
            skCircle(sketch, "E12.17.8.0", {"center": v(466, -494.7) * mm, "radius": 4.5 * mm});
            skCircle(sketch, "E12.17.9.0", {"center": v(466, -483.1) * mm, "radius": 4.5 * mm});
            skCircle(sketch, "E12.17.10.0", {"center": v(466, -471.5) * mm, "radius": 4.5 * mm});
            skCircle(sketch, "E12.17.11.0", {"center": v(466, -459.9) * mm, "radius": 4.5 * mm});
            skCircle(sketch, "E12.17.12.0", {"center": v(466, -448.3) * mm, "radius": 4.5 * mm});
            skCircle(sketch, "E12.17.13.0", {"center": v(466, -436.7) * mm, "radius": 4.5 * mm});
            skCircle(sketch, "E12.17.14.0", {"center": v(466, -425.1) * mm, "radius": 4.5 * mm});
            skCircle(sketch, "E12.17.15.0", {"center": v(466, -413.5) * mm, "radius": 4.5 * mm});
            skCircle(sketch, "E12.17.16.0", {"center": v(466, -401.9) * mm, "radius": 4.5 * mm});
            skCircle(sketch, "E12.18.0.0", {"center": v(477.6, -587.5) * mm, "radius": 4.5 * mm});
            skCircle(sketch, "E12.18.1.0", {"center": v(477.6, -575.9) * mm, "radius": 4.5 * mm});
            skCircle(sketch, "E12.18.2.0", {"center": v(477.6, -564.3) * mm, "radius": 4.5 * mm});
            skCircle(sketch, "E12.18.3.0", {"center": v(477.6, -552.7) * mm, "radius": 4.5 * mm});
            skCircle(sketch, "E12.18.4.0", {"center": v(477.6, -541.1) * mm, "radius": 4.5 * mm});
            skCircle(sketch, "E12.18.5.0", {"center": v(477.6, -529.5) * mm, "radius": 4.5 * mm});
            skCircle(sketch, "E12.18.6.0", {"center": v(477.6, -517.9) * mm, "radius": 4.5 * mm});
            skCircle(sketch, "E12.18.7.0", {"center": v(477.6, -506.3) * mm, "radius": 4.5 * mm});
            skCircle(sketch, "E12.18.8.0", {"center": v(477.6, -494.7) * mm, "radius": 4.5 * mm});
            skCircle(sketch, "E12.18.9.0", {"center": v(477.6, -483.1) * mm, "radius": 4.5 * mm});
            skCircle(sketch, "E12.18.10.0", {"center": v(477.6, -471.5) * mm, "radius": 4.5 * mm});
            skCircle(sketch, "E12.18.11.0", {"center": v(477.6, -459.9) * mm, "radius": 4.5 * mm});
            skCircle(sketch, "E12.18.12.0", {"center": v(477.6, -448.3) * mm, "radius": 4.5 * mm});
            skCircle(sketch, "E12.18.13.0", {"center": v(477.6, -436.7) * mm, "radius": 4.5 * mm});
            skCircle(sketch, "E12.18.14.0", {"center": v(477.6, -425.1) * mm, "radius": 4.5 * mm});
            skCircle(sketch, "E12.18.15.0", {"center": v(477.6, -413.5) * mm, "radius": 4.5 * mm});
            skCircle(sketch, "E12.18.16.0", {"center": v(477.6, -401.9) * mm, "radius": 4.5 * mm});
            skCircle(sketch, "E12.19.0.0", {"center": v(489.2, -587.5) * mm, "radius": 4.5 * mm});
            skCircle(sketch, "E12.19.1.0", {"center": v(489.2, -575.9) * mm, "radius": 4.5 * mm});
            skCircle(sketch, "E12.19.2.0", {"center": v(489.2, -564.3) * mm, "radius": 4.5 * mm});
            skCircle(sketch, "E12.19.3.0", {"center": v(489.2, -552.7) * mm, "radius": 4.5 * mm});
            skCircle(sketch, "E12.19.4.0", {"center": v(489.2, -541.1) * mm, "radius": 4.5 * mm});
            skCircle(sketch, "E12.19.5.0", {"center": v(489.2, -529.5) * mm, "radius": 4.5 * mm});
            skCircle(sketch, "E12.19.6.0", {"center": v(489.2, -517.9) * mm, "radius": 4.5 * mm});
            skCircle(sketch, "E12.19.7.0", {"center": v(489.2, -506.3) * mm, "radius": 4.5 * mm});
            skCircle(sketch, "E12.19.8.0", {"center": v(489.2, -494.7) * mm, "radius": 4.5 * mm});
            skCircle(sketch, "E12.19.9.0", {"center": v(489.2, -483.1) * mm, "radius": 4.5 * mm});
            skCircle(sketch, "E12.19.10.0", {"center": v(489.2, -471.5) * mm, "radius": 4.5 * mm});
            skCircle(sketch, "E12.19.11.0", {"center": v(489.2, -459.9) * mm, "radius": 4.5 * mm});
            skCircle(sketch, "E12.19.12.0", {"center": v(489.2, -448.3) * mm, "radius": 4.5 * mm});
            skCircle(sketch, "E12.19.13.0", {"center": v(489.2, -436.7) * mm, "radius": 4.5 * mm});
            skCircle(sketch, "E12.19.14.0", {"center": v(489.2, -425.1) * mm, "radius": 4.5 * mm});
            skCircle(sketch, "E12.19.15.0", {"center": v(489.2, -413.5) * mm, "radius": 4.5 * mm});
            skCircle(sketch, "E12.19.16.0", {"center": v(489.2, -401.9) * mm, "radius": 4.5 * mm});
            skCircle(sketch, "E12.20.0.0", {"center": v(500.8, -587.5) * mm, "radius": 4.5 * mm});
            skCircle(sketch, "E12.20.1.0", {"center": v(500.8, -575.9) * mm, "radius": 4.5 * mm});
            skCircle(sketch, "E12.20.2.0", {"center": v(500.8, -564.3) * mm, "radius": 4.5 * mm});
            skCircle(sketch, "E12.20.3.0", {"center": v(500.8, -552.7) * mm, "radius": 4.5 * mm});
            skCircle(sketch, "E12.20.4.0", {"center": v(500.8, -541.1) * mm, "radius": 4.5 * mm});
            skCircle(sketch, "E12.20.5.0", {"center": v(500.8, -529.5) * mm, "radius": 4.5 * mm});
            skCircle(sketch, "E12.20.6.0", {"center": v(500.8, -517.9) * mm, "radius": 4.5 * mm});
            skCircle(sketch, "E12.20.7.0", {"center": v(500.8, -506.3) * mm, "radius": 4.5 * mm});
            skCircle(sketch, "E12.20.8.0", {"center": v(500.8, -494.7) * mm, "radius": 4.5 * mm});
            skCircle(sketch, "E12.20.9.0", {"center": v(500.8, -483.1) * mm, "radius": 4.5 * mm});
            skCircle(sketch, "E12.20.10.0", {"center": v(500.8, -471.5) * mm, "radius": 4.5 * mm});
            skCircle(sketch, "E12.20.11.0", {"center": v(500.8, -459.9) * mm, "radius": 4.5 * mm});
            skCircle(sketch, "E12.20.12.0", {"center": v(500.8, -448.3) * mm, "radius": 4.5 * mm});
            skCircle(sketch, "E12.20.13.0", {"center": v(500.8, -436.7) * mm, "radius": 4.5 * mm});
            skCircle(sketch, "E12.20.14.0", {"center": v(500.8, -425.1) * mm, "radius": 4.5 * mm});
            skCircle(sketch, "E12.20.15.0", {"center": v(500.8, -413.5) * mm, "radius": 4.5 * mm});
            skCircle(sketch, "E12.20.16.0", {"center": v(500.8, -401.9) * mm, "radius": 4.5 * mm});
            skCircle(sketch, "E12.21.0.0", {"center": v(512.4, -587.5) * mm, "radius": 4.5 * mm});
            skCircle(sketch, "E12.21.1.0", {"center": v(512.4, -575.9) * mm, "radius": 4.5 * mm});
            skCircle(sketch, "E12.21.2.0", {"center": v(512.4, -564.3) * mm, "radius": 4.5 * mm});
            skCircle(sketch, "E12.21.3.0", {"center": v(512.4, -552.7) * mm, "radius": 4.5 * mm});
            skCircle(sketch, "E12.21.4.0", {"center": v(512.4, -541.1) * mm, "radius": 4.5 * mm});
            skCircle(sketch, "E12.21.5.0", {"center": v(512.4, -529.5) * mm, "radius": 4.5 * mm});
            skCircle(sketch, "E12.21.6.0", {"center": v(512.4, -517.9) * mm, "radius": 4.5 * mm});
            skCircle(sketch, "E12.21.7.0", {"center": v(512.4, -506.3) * mm, "radius": 4.5 * mm});
            skCircle(sketch, "E12.21.8.0", {"center": v(512.4, -494.7) * mm, "radius": 4.5 * mm});
            skCircle(sketch, "E12.21.9.0", {"center": v(512.4, -483.1) * mm, "radius": 4.5 * mm});
            skCircle(sketch, "E12.21.10.0", {"center": v(512.4, -471.5) * mm, "radius": 4.5 * mm});
            skCircle(sketch, "E12.21.11.0", {"center": v(512.4, -459.9) * mm, "radius": 4.5 * mm});
            skCircle(sketch, "E12.21.12.0", {"center": v(512.4, -448.3) * mm, "radius": 4.5 * mm});
            skCircle(sketch, "E12.21.13.0", {"center": v(512.4, -436.7) * mm, "radius": 4.5 * mm});
            skCircle(sketch, "E12.21.14.0", {"center": v(512.4, -425.1) * mm, "radius": 4.5 * mm});
            skCircle(sketch, "E12.21.15.0", {"center": v(512.4, -413.5) * mm, "radius": 4.5 * mm});
            skCircle(sketch, "E12.21.16.0", {"center": v(512.4, -401.9) * mm, "radius": 4.5 * mm});
            skCircle(sketch, "E12.22.0.0", {"center": v(524, -587.5) * mm, "radius": 4.5 * mm});
            skCircle(sketch, "E12.22.1.0", {"center": v(524, -575.9) * mm, "radius": 4.5 * mm});
            skCircle(sketch, "E12.22.2.0", {"center": v(524, -564.3) * mm, "radius": 4.5 * mm});
            skCircle(sketch, "E12.22.3.0", {"center": v(524, -552.7) * mm, "radius": 4.5 * mm});
            skCircle(sketch, "E12.22.4.0", {"center": v(524, -541.1) * mm, "radius": 4.5 * mm});
            skCircle(sketch, "E12.22.5.0", {"center": v(524, -529.5) * mm, "radius": 4.5 * mm});
            skCircle(sketch, "E12.22.6.0", {"center": v(524, -517.9) * mm, "radius": 4.5 * mm});
            skCircle(sketch, "E12.22.7.0", {"center": v(524, -506.3) * mm, "radius": 4.5 * mm});
            skCircle(sketch, "E12.22.8.0", {"center": v(524, -494.7) * mm, "radius": 4.5 * mm});
            skCircle(sketch, "E12.22.9.0", {"center": v(524, -483.1) * mm, "radius": 4.5 * mm});
            skCircle(sketch, "E12.22.10.0", {"center": v(524, -471.5) * mm, "radius": 4.5 * mm});
            skCircle(sketch, "E12.22.11.0", {"center": v(524, -459.9) * mm, "radius": 4.5 * mm});
            skCircle(sketch, "E12.22.12.0", {"center": v(524, -448.3) * mm, "radius": 4.5 * mm});
            skCircle(sketch, "E12.22.13.0", {"center": v(524, -436.7) * mm, "radius": 4.5 * mm});
            skCircle(sketch, "E12.22.14.0", {"center": v(524, -425.1) * mm, "radius": 4.5 * mm});
            skCircle(sketch, "E12.22.15.0", {"center": v(524, -413.5) * mm, "radius": 4.5 * mm});
            skCircle(sketch, "E12.22.16.0", {"center": v(524, -401.9) * mm, "radius": 4.5 * mm});
            skCircle(sketch, "E12.23.0.0", {"center": v(535.6, -587.5) * mm, "radius": 4.5 * mm});
            skCircle(sketch, "E12.23.1.0", {"center": v(535.6, -575.9) * mm, "radius": 4.5 * mm});
            skCircle(sketch, "E12.23.2.0", {"center": v(535.6, -564.3) * mm, "radius": 4.5 * mm});
            skCircle(sketch, "E12.23.3.0", {"center": v(535.6, -552.7) * mm, "radius": 4.5 * mm});
            skCircle(sketch, "E12.23.4.0", {"center": v(535.6, -541.1) * mm, "radius": 4.5 * mm});
            skCircle(sketch, "E12.23.5.0", {"center": v(535.6, -529.5) * mm, "radius": 4.5 * mm});
            skCircle(sketch, "E12.23.6.0", {"center": v(535.6, -517.9) * mm, "radius": 4.5 * mm});
            skCircle(sketch, "E12.23.7.0", {"center": v(535.6, -506.3) * mm, "radius": 4.5 * mm});
            skCircle(sketch, "E12.23.8.0", {"center": v(535.6, -494.7) * mm, "radius": 4.5 * mm});
            skCircle(sketch, "E12.23.9.0", {"center": v(535.6, -483.1) * mm, "radius": 4.5 * mm});
            skCircle(sketch, "E12.23.10.0", {"center": v(535.6, -471.5) * mm, "radius": 4.5 * mm});
            skCircle(sketch, "E12.23.11.0", {"center": v(535.6, -459.9) * mm, "radius": 4.5 * mm});
            skCircle(sketch, "E12.23.12.0", {"center": v(535.6, -448.3) * mm, "radius": 4.5 * mm});
            skCircle(sketch, "E12.23.13.0", {"center": v(535.6, -436.7) * mm, "radius": 4.5 * mm});
            skCircle(sketch, "E12.23.14.0", {"center": v(535.6, -425.1) * mm, "radius": 4.5 * mm});
            skCircle(sketch, "E12.23.15.0", {"center": v(535.6, -413.5) * mm, "radius": 4.5 * mm});
            skCircle(sketch, "E12.23.16.0", {"center": v(535.6, -401.9) * mm, "radius": 4.5 * mm});
            skCircle(sketch, "E12.24.0.0", {"center": v(547.2, -587.5) * mm, "radius": 4.5 * mm});
            skCircle(sketch, "E12.24.1.0", {"center": v(547.2, -575.9) * mm, "radius": 4.5 * mm});
            skCircle(sketch, "E12.24.2.0", {"center": v(547.2, -564.3) * mm, "radius": 4.5 * mm});
            skCircle(sketch, "E12.24.3.0", {"center": v(547.2, -552.7) * mm, "radius": 4.5 * mm});
            skCircle(sketch, "E12.24.4.0", {"center": v(547.2, -541.1) * mm, "radius": 4.5 * mm});
            skCircle(sketch, "E12.24.5.0", {"center": v(547.2, -529.5) * mm, "radius": 4.5 * mm});
            skCircle(sketch, "E12.24.6.0", {"center": v(547.2, -517.9) * mm, "radius": 4.5 * mm});
            skCircle(sketch, "E12.24.7.0", {"center": v(547.2, -506.3) * mm, "radius": 4.5 * mm});
            skCircle(sketch, "E12.24.8.0", {"center": v(547.2, -494.7) * mm, "radius": 4.5 * mm});
            skCircle(sketch, "E12.24.9.0", {"center": v(547.2, -483.1) * mm, "radius": 4.5 * mm});
            skCircle(sketch, "E12.24.10.0", {"center": v(547.2, -471.5) * mm, "radius": 4.5 * mm});
            skCircle(sketch, "E12.24.11.0", {"center": v(547.2, -459.9) * mm, "radius": 4.5 * mm});
            skCircle(sketch, "E12.24.12.0", {"center": v(547.2, -448.3) * mm, "radius": 4.5 * mm});
            skCircle(sketch, "E12.24.13.0", {"center": v(547.2, -436.7) * mm, "radius": 4.5 * mm});
            skCircle(sketch, "E12.24.14.0", {"center": v(547.2, -425.1) * mm, "radius": 4.5 * mm});
            skCircle(sketch, "E12.24.15.0", {"center": v(547.2, -413.5) * mm, "radius": 4.5 * mm});
            skCircle(sketch, "E12.24.16.0", {"center": v(547.2, -401.9) * mm, "radius": 4.5 * mm});
            skCircle(sketch, "E12.25.0.0", {"center": v(558.8, -587.5) * mm, "radius": 4.5 * mm});
            skCircle(sketch, "E12.25.1.0", {"center": v(558.8, -575.9) * mm, "radius": 4.5 * mm});
            skCircle(sketch, "E12.25.2.0", {"center": v(558.8, -564.3) * mm, "radius": 4.5 * mm});
            skCircle(sketch, "E12.25.3.0", {"center": v(558.8, -552.7) * mm, "radius": 4.5 * mm});
            skCircle(sketch, "E12.25.4.0", {"center": v(558.8, -541.1) * mm, "radius": 4.5 * mm});
            skCircle(sketch, "E12.25.5.0", {"center": v(558.8, -529.5) * mm, "radius": 4.5 * mm});
            skCircle(sketch, "E12.25.6.0", {"center": v(558.8, -517.9) * mm, "radius": 4.5 * mm});
            skCircle(sketch, "E12.25.7.0", {"center": v(558.8, -506.3) * mm, "radius": 4.5 * mm});
            skCircle(sketch, "E12.25.8.0", {"center": v(558.8, -494.7) * mm, "radius": 4.5 * mm});
            skCircle(sketch, "E12.25.9.0", {"center": v(558.8, -483.1) * mm, "radius": 4.5 * mm});
            skCircle(sketch, "E12.25.10.0", {"center": v(558.8, -471.5) * mm, "radius": 4.5 * mm});
            skCircle(sketch, "E12.25.11.0", {"center": v(558.8, -459.9) * mm, "radius": 4.5 * mm});
            skCircle(sketch, "E12.25.12.0", {"center": v(558.8, -448.3) * mm, "radius": 4.5 * mm});
            skCircle(sketch, "E12.25.13.0", {"center": v(558.8, -436.7) * mm, "radius": 4.5 * mm});
            skCircle(sketch, "E12.25.14.0", {"center": v(558.8, -425.1) * mm, "radius": 4.5 * mm});
            skCircle(sketch, "E12.25.15.0", {"center": v(558.8, -413.5) * mm, "radius": 4.5 * mm});
            skCircle(sketch, "E12.25.16.0", {"center": v(558.8, -401.9) * mm, "radius": 4.5 * mm});
            skCircle(sketch, "E12.26.0.0", {"center": v(570.4, -587.5) * mm, "radius": 4.5 * mm});
            skCircle(sketch, "E12.26.1.0", {"center": v(570.4, -575.9) * mm, "radius": 4.5 * mm});
            skCircle(sketch, "E12.26.2.0", {"center": v(570.4, -564.3) * mm, "radius": 4.5 * mm});
            skCircle(sketch, "E12.26.3.0", {"center": v(570.4, -552.7) * mm, "radius": 4.5 * mm});
            skCircle(sketch, "E12.26.4.0", {"center": v(570.4, -541.1) * mm, "radius": 4.5 * mm});
            skCircle(sketch, "E12.26.5.0", {"center": v(570.4, -529.5) * mm, "radius": 4.5 * mm});
            skCircle(sketch, "E12.26.6.0", {"center": v(570.4, -517.9) * mm, "radius": 4.5 * mm});
            skCircle(sketch, "E12.26.7.0", {"center": v(570.4, -506.3) * mm, "radius": 4.5 * mm});
            skCircle(sketch, "E12.26.8.0", {"center": v(570.4, -494.7) * mm, "radius": 4.5 * mm});
            skCircle(sketch, "E12.26.9.0", {"center": v(570.4, -483.1) * mm, "radius": 4.5 * mm});
            skCircle(sketch, "E12.26.10.0", {"center": v(570.4, -471.5) * mm, "radius": 4.5 * mm});
            skCircle(sketch, "E12.26.11.0", {"center": v(570.4, -459.9) * mm, "radius": 4.5 * mm});
            skCircle(sketch, "E12.26.12.0", {"center": v(570.4, -448.3) * mm, "radius": 4.5 * mm});
            skCircle(sketch, "E12.26.13.0", {"center": v(570.4, -436.7) * mm, "radius": 4.5 * mm});
            skCircle(sketch, "E12.26.14.0", {"center": v(570.4, -425.1) * mm, "radius": 4.5 * mm});
            skCircle(sketch, "E12.26.15.0", {"center": v(570.4, -413.5) * mm, "radius": 4.5 * mm});
            skCircle(sketch, "E12.26.16.0", {"center": v(570.4, -401.9) * mm, "radius": 4.5 * mm});
            skCircle(sketch, "E12.27.0.0", {"center": v(582, -587.5) * mm, "radius": 4.5 * mm});
            skCircle(sketch, "E12.27.1.0", {"center": v(582, -575.9) * mm, "radius": 4.5 * mm});
            skCircle(sketch, "E12.27.2.0", {"center": v(582, -564.3) * mm, "radius": 4.5 * mm});
            skCircle(sketch, "E12.27.3.0", {"center": v(582, -552.7) * mm, "radius": 4.5 * mm});
            skCircle(sketch, "E12.27.4.0", {"center": v(582, -541.1) * mm, "radius": 4.5 * mm});
            skCircle(sketch, "E12.27.5.0", {"center": v(582, -529.5) * mm, "radius": 4.5 * mm});
            skCircle(sketch, "E12.27.6.0", {"center": v(582, -517.9) * mm, "radius": 4.5 * mm});
            skCircle(sketch, "E12.27.7.0", {"center": v(582, -506.3) * mm, "radius": 4.5 * mm});
            skCircle(sketch, "E12.27.8.0", {"center": v(582, -494.7) * mm, "radius": 4.5 * mm});
            skCircle(sketch, "E12.27.9.0", {"center": v(582, -483.1) * mm, "radius": 4.5 * mm});
            skCircle(sketch, "E12.27.10.0", {"center": v(582, -471.5) * mm, "radius": 4.5 * mm});
            skCircle(sketch, "E12.27.11.0", {"center": v(582, -459.9) * mm, "radius": 4.5 * mm});
            skCircle(sketch, "E12.27.12.0", {"center": v(582, -448.3) * mm, "radius": 4.5 * mm});
            skCircle(sketch, "E12.27.13.0", {"center": v(582, -436.7) * mm, "radius": 4.5 * mm});
            skCircle(sketch, "E12.27.14.0", {"center": v(582, -425.1) * mm, "radius": 4.5 * mm});
            skCircle(sketch, "E12.27.15.0", {"center": v(582, -413.5) * mm, "radius": 4.5 * mm});
            skCircle(sketch, "E12.27.16.0", {"center": v(582, -401.9) * mm, "radius": 4.5 * mm});
            skCircle(sketch, "E12.28.0.0", {"center": v(593.6, -587.5) * mm, "radius": 4.5 * mm});
            skCircle(sketch, "E12.28.1.0", {"center": v(593.6, -575.9) * mm, "radius": 4.5 * mm});
            skCircle(sketch, "E12.28.2.0", {"center": v(593.6, -564.3) * mm, "radius": 4.5 * mm});
            skCircle(sketch, "E12.28.3.0", {"center": v(593.6, -552.7) * mm, "radius": 4.5 * mm});
            skCircle(sketch, "E12.28.4.0", {"center": v(593.6, -541.1) * mm, "radius": 4.5 * mm});
            skCircle(sketch, "E12.28.5.0", {"center": v(593.6, -529.5) * mm, "radius": 4.5 * mm});
            skCircle(sketch, "E12.28.6.0", {"center": v(593.6, -517.9) * mm, "radius": 4.5 * mm});
            skCircle(sketch, "E12.28.7.0", {"center": v(593.6, -506.3) * mm, "radius": 4.5 * mm});
            skCircle(sketch, "E12.28.8.0", {"center": v(593.6, -494.7) * mm, "radius": 4.5 * mm});
            skCircle(sketch, "E12.28.9.0", {"center": v(593.6, -483.1) * mm, "radius": 4.5 * mm});
            skCircle(sketch, "E12.28.10.0", {"center": v(593.6, -471.5) * mm, "radius": 4.5 * mm});
            skCircle(sketch, "E12.28.11.0", {"center": v(593.6, -459.9) * mm, "radius": 4.5 * mm});
            skCircle(sketch, "E12.28.12.0", {"center": v(593.6, -448.3) * mm, "radius": 4.5 * mm});
            skCircle(sketch, "E12.28.13.0", {"center": v(593.6, -436.7) * mm, "radius": 4.5 * mm});
            skCircle(sketch, "E12.28.14.0", {"center": v(593.6, -425.1) * mm, "radius": 4.5 * mm});
            skCircle(sketch, "E12.28.15.0", {"center": v(593.6, -413.5) * mm, "radius": 4.5 * mm});
            skCircle(sketch, "E12.28.16.0", {"center": v(593.6, -401.9) * mm, "radius": 4.5 * mm});
            skCircle(sketch, "E12.29.0.0", {"center": v(605.2, -587.5) * mm, "radius": 4.5 * mm});
            skCircle(sketch, "E12.29.1.0", {"center": v(605.2, -575.9) * mm, "radius": 4.5 * mm});
            skCircle(sketch, "E12.29.2.0", {"center": v(605.2, -564.3) * mm, "radius": 4.5 * mm});
            skCircle(sketch, "E12.29.3.0", {"center": v(605.2, -552.7) * mm, "radius": 4.5 * mm});
            skCircle(sketch, "E12.29.4.0", {"center": v(605.2, -541.1) * mm, "radius": 4.5 * mm});
            skCircle(sketch, "E12.29.5.0", {"center": v(605.2, -529.5) * mm, "radius": 4.5 * mm});
            skCircle(sketch, "E12.29.6.0", {"center": v(605.2, -517.9) * mm, "radius": 4.5 * mm});
            skCircle(sketch, "E12.29.7.0", {"center": v(605.2, -506.3) * mm, "radius": 4.5 * mm});
            skCircle(sketch, "E12.29.8.0", {"center": v(605.2, -494.7) * mm, "radius": 4.5 * mm});
            skCircle(sketch, "E12.29.9.0", {"center": v(605.2, -483.1) * mm, "radius": 4.5 * mm});
            skCircle(sketch, "E12.29.10.0", {"center": v(605.2, -471.5) * mm, "radius": 4.5 * mm});
            skCircle(sketch, "E12.29.11.0", {"center": v(605.2, -459.9) * mm, "radius": 4.5 * mm});
            skCircle(sketch, "E12.29.12.0", {"center": v(605.2, -448.3) * mm, "radius": 4.5 * mm});
            skCircle(sketch, "E12.29.13.0", {"center": v(605.2, -436.7) * mm, "radius": 4.5 * mm});
            skCircle(sketch, "E12.29.14.0", {"center": v(605.2, -425.1) * mm, "radius": 4.5 * mm});
            skCircle(sketch, "E12.29.15.0", {"center": v(605.2, -413.5) * mm, "radius": 4.5 * mm});
            skCircle(sketch, "E12.29.16.0", {"center": v(605.2, -401.9) * mm, "radius": 4.5 * mm});
            skLineSegment(sketch, "E12.direction1", {"start": v(268.8, -587.5) * mm, "end": v(280.4, -587.5) * mm, "construction": true});
            skLineSegment(sketch, "E12.direction2", {"start": v(268.8, -587.5) * mm, "end": v(268.8, -575.9) * mm, "construction": true});
            skSolve(sketch);
        }
        {
            var Q0;
            Q0 = qSketchRegion(id + "F11", true);
            extrude(context, id + "F12", {"entities" : qUnion([Q0]), "operationType" : NewBodyOperationType.REMOVE, "oppositeDirection" : true, "depth" : 25 * mm});
        }
        {
            var Q0;
            Q0=makeQuery(id+"F9.opExtrude","CAP_FACE",FACE,{"disambiguationData":[OSD([sQuery(id+"F8.wireOp",EDGE,"E10.bottom"),sQuery(id+"F8.wireOp",EDGE,"E10.top"),sQuery(id+"F8.wireOp",EDGE,"E10.left"),sQuery(id+"F8.wireOp",EDGE,"E10.right")])],"isStart":false});
            var sketch = newSketch(context, id + "F13", { "sketchPlane" : qUnion([Q0])});
            skCircle(sketch, "E13", {"center": v(268.8, -287.4) * mm, "radius": 4.5 * mm});
            skCircle(sketch, "E14.0.1.0", {"center": v(268.8, -275.8) * mm, "radius": 4.5 * mm});
            skCircle(sketch, "E14.0.2.0", {"center": v(268.8, -264.2) * mm, "radius": 4.5 * mm});
            skCircle(sketch, "E14.0.3.0", {"center": v(268.8, -252.6) * mm, "radius": 4.5 * mm});
            skCircle(sketch, "E14.0.4.0", {"center": v(268.8, -241) * mm, "radius": 4.5 * mm});
            skCircle(sketch, "E14.0.5.0", {"center": v(268.8, -229.4) * mm, "radius": 4.5 * mm});
            skCircle(sketch, "E14.0.6.0", {"center": v(268.8, -217.8) * mm, "radius": 4.5 * mm});
            skCircle(sketch, "E14.0.7.0", {"center": v(268.8, -206.2) * mm, "radius": 4.5 * mm});
            skCircle(sketch, "E14.0.8.0", {"center": v(268.8, -194.6) * mm, "radius": 4.5 * mm});
            skCircle(sketch, "E14.0.9.0", {"center": v(268.8, -183) * mm, "radius": 4.5 * mm});
            skCircle(sketch, "E14.0.10.0", {"center": v(268.8, -171.4) * mm, "radius": 4.5 * mm});
            skCircle(sketch, "E14.0.11.0", {"center": v(268.8, -159.8) * mm, "radius": 4.5 * mm});
            skCircle(sketch, "E14.0.12.0", {"center": v(268.8, -148.2) * mm, "radius": 4.5 * mm});
            skCircle(sketch, "E14.1.0.0", {"center": v(280.4, -287.4) * mm, "radius": 4.5 * mm});
            skCircle(sketch, "E14.1.1.0", {"center": v(280.4, -275.8) * mm, "radius": 4.5 * mm});
            skCircle(sketch, "E14.1.2.0", {"center": v(280.4, -264.2) * mm, "radius": 4.5 * mm});
            skCircle(sketch, "E14.1.3.0", {"center": v(280.4, -252.6) * mm, "radius": 4.5 * mm});
            skCircle(sketch, "E14.1.4.0", {"center": v(280.4, -241) * mm, "radius": 4.5 * mm});
            skCircle(sketch, "E14.1.5.0", {"center": v(280.4, -229.4) * mm, "radius": 4.5 * mm});
            skCircle(sketch, "E14.1.6.0", {"center": v(280.4, -217.8) * mm, "radius": 4.5 * mm});
            skCircle(sketch, "E14.1.7.0", {"center": v(280.4, -206.2) * mm, "radius": 4.5 * mm});
            skCircle(sketch, "E14.1.8.0", {"center": v(280.4, -194.6) * mm, "radius": 4.5 * mm});
            skCircle(sketch, "E14.1.9.0", {"center": v(280.4, -183) * mm, "radius": 4.5 * mm});
            skCircle(sketch, "E14.1.10.0", {"center": v(280.4, -171.4) * mm, "radius": 4.5 * mm});
            skCircle(sketch, "E14.1.11.0", {"center": v(280.4, -159.8) * mm, "radius": 4.5 * mm});
            skCircle(sketch, "E14.1.12.0", {"center": v(280.4, -148.2) * mm, "radius": 4.5 * mm});
            skCircle(sketch, "E14.2.0.0", {"center": v(292, -287.4) * mm, "radius": 4.5 * mm});
            skCircle(sketch, "E14.2.1.0", {"center": v(292, -275.8) * mm, "radius": 4.5 * mm});
            skCircle(sketch, "E14.2.2.0", {"center": v(292, -264.2) * mm, "radius": 4.5 * mm});
            skCircle(sketch, "E14.2.3.0", {"center": v(292, -252.6) * mm, "radius": 4.5 * mm});
            skCircle(sketch, "E14.2.4.0", {"center": v(292, -241) * mm, "radius": 4.5 * mm});
            skCircle(sketch, "E14.2.5.0", {"center": v(292, -229.4) * mm, "radius": 4.5 * mm});
            skCircle(sketch, "E14.2.6.0", {"center": v(292, -217.8) * mm, "radius": 4.5 * mm});
            skCircle(sketch, "E14.2.7.0", {"center": v(292, -206.2) * mm, "radius": 4.5 * mm});
            skCircle(sketch, "E14.2.8.0", {"center": v(292, -194.6) * mm, "radius": 4.5 * mm});
            skCircle(sketch, "E14.2.9.0", {"center": v(292, -183) * mm, "radius": 4.5 * mm});
            skCircle(sketch, "E14.2.10.0", {"center": v(292, -171.4) * mm, "radius": 4.5 * mm});
            skCircle(sketch, "E14.2.11.0", {"center": v(292, -159.8) * mm, "radius": 4.5 * mm});
            skCircle(sketch, "E14.2.12.0", {"center": v(292, -148.2) * mm, "radius": 4.5 * mm});
            skCircle(sketch, "E14.3.0.0", {"center": v(303.6, -287.4) * mm, "radius": 4.5 * mm});
            skCircle(sketch, "E14.3.1.0", {"center": v(303.6, -275.8) * mm, "radius": 4.5 * mm});
            skCircle(sketch, "E14.3.2.0", {"center": v(303.6, -264.2) * mm, "radius": 4.5 * mm});
            skCircle(sketch, "E14.3.3.0", {"center": v(303.6, -252.6) * mm, "radius": 4.5 * mm});
            skCircle(sketch, "E14.3.4.0", {"center": v(303.6, -241) * mm, "radius": 4.5 * mm});
            skCircle(sketch, "E14.3.5.0", {"center": v(303.6, -229.4) * mm, "radius": 4.5 * mm});
            skCircle(sketch, "E14.3.6.0", {"center": v(303.6, -217.8) * mm, "radius": 4.5 * mm});
            skCircle(sketch, "E14.3.7.0", {"center": v(303.6, -206.2) * mm, "radius": 4.5 * mm});
            skCircle(sketch, "E14.3.8.0", {"center": v(303.6, -194.6) * mm, "radius": 4.5 * mm});
            skCircle(sketch, "E14.3.9.0", {"center": v(303.6, -183) * mm, "radius": 4.5 * mm});
            skCircle(sketch, "E14.3.10.0", {"center": v(303.6, -171.4) * mm, "radius": 4.5 * mm});
            skCircle(sketch, "E14.3.11.0", {"center": v(303.6, -159.8) * mm, "radius": 4.5 * mm});
            skCircle(sketch, "E14.3.12.0", {"center": v(303.6, -148.2) * mm, "radius": 4.5 * mm});
            skCircle(sketch, "E14.4.0.0", {"center": v(315.2, -287.4) * mm, "radius": 4.5 * mm});
            skCircle(sketch, "E14.4.1.0", {"center": v(315.2, -275.8) * mm, "radius": 4.5 * mm});
            skCircle(sketch, "E14.4.2.0", {"center": v(315.2, -264.2) * mm, "radius": 4.5 * mm});
            skCircle(sketch, "E14.4.3.0", {"center": v(315.2, -252.6) * mm, "radius": 4.5 * mm});
            skCircle(sketch, "E14.4.4.0", {"center": v(315.2, -241) * mm, "radius": 4.5 * mm});
            skCircle(sketch, "E14.4.5.0", {"center": v(315.2, -229.4) * mm, "radius": 4.5 * mm});
            skCircle(sketch, "E14.4.6.0", {"center": v(315.2, -217.8) * mm, "radius": 4.5 * mm});
            skCircle(sketch, "E14.4.7.0", {"center": v(315.2, -206.2) * mm, "radius": 4.5 * mm});
            skCircle(sketch, "E14.4.8.0", {"center": v(315.2, -194.6) * mm, "radius": 4.5 * mm});
            skCircle(sketch, "E14.4.9.0", {"center": v(315.2, -183) * mm, "radius": 4.5 * mm});
            skCircle(sketch, "E14.4.10.0", {"center": v(315.2, -171.4) * mm, "radius": 4.5 * mm});
            skCircle(sketch, "E14.4.11.0", {"center": v(315.2, -159.8) * mm, "radius": 4.5 * mm});
            skCircle(sketch, "E14.4.12.0", {"center": v(315.2, -148.2) * mm, "radius": 4.5 * mm});
            skCircle(sketch, "E14.5.0.0", {"center": v(326.8, -287.4) * mm, "radius": 4.5 * mm});
            skCircle(sketch, "E14.5.1.0", {"center": v(326.8, -275.8) * mm, "radius": 4.5 * mm});
            skCircle(sketch, "E14.5.2.0", {"center": v(326.8, -264.2) * mm, "radius": 4.5 * mm});
            skCircle(sketch, "E14.5.3.0", {"center": v(326.8, -252.6) * mm, "radius": 4.5 * mm});
            skCircle(sketch, "E14.5.4.0", {"center": v(326.8, -241) * mm, "radius": 4.5 * mm});
            skCircle(sketch, "E14.5.5.0", {"center": v(326.8, -229.4) * mm, "radius": 4.5 * mm});
            skCircle(sketch, "E14.5.6.0", {"center": v(326.8, -217.8) * mm, "radius": 4.5 * mm});
            skCircle(sketch, "E14.5.7.0", {"center": v(326.8, -206.2) * mm, "radius": 4.5 * mm});
            skCircle(sketch, "E14.5.8.0", {"center": v(326.8, -194.6) * mm, "radius": 4.5 * mm});
            skCircle(sketch, "E14.5.9.0", {"center": v(326.8, -183) * mm, "radius": 4.5 * mm});
            skCircle(sketch, "E14.5.10.0", {"center": v(326.8, -171.4) * mm, "radius": 4.5 * mm});
            skCircle(sketch, "E14.5.11.0", {"center": v(326.8, -159.8) * mm, "radius": 4.5 * mm});
            skCircle(sketch, "E14.5.12.0", {"center": v(326.8, -148.2) * mm, "radius": 4.5 * mm});
            skCircle(sketch, "E14.6.0.0", {"center": v(338.4, -287.4) * mm, "radius": 4.5 * mm});
            skCircle(sketch, "E14.6.1.0", {"center": v(338.4, -275.8) * mm, "radius": 4.5 * mm});
            skCircle(sketch, "E14.6.2.0", {"center": v(338.4, -264.2) * mm, "radius": 4.5 * mm});
            skCircle(sketch, "E14.6.3.0", {"center": v(338.4, -252.6) * mm, "radius": 4.5 * mm});
            skCircle(sketch, "E14.6.4.0", {"center": v(338.4, -241) * mm, "radius": 4.5 * mm});
            skCircle(sketch, "E14.6.5.0", {"center": v(338.4, -229.4) * mm, "radius": 4.5 * mm});
            skCircle(sketch, "E14.6.6.0", {"center": v(338.4, -217.8) * mm, "radius": 4.5 * mm});
            skCircle(sketch, "E14.6.7.0", {"center": v(338.4, -206.2) * mm, "radius": 4.5 * mm});
            skCircle(sketch, "E14.6.8.0", {"center": v(338.4, -194.6) * mm, "radius": 4.5 * mm});
            skCircle(sketch, "E14.6.9.0", {"center": v(338.4, -183) * mm, "radius": 4.5 * mm});
            skCircle(sketch, "E14.6.10.0", {"center": v(338.4, -171.4) * mm, "radius": 4.5 * mm});
            skCircle(sketch, "E14.6.11.0", {"center": v(338.4, -159.8) * mm, "radius": 4.5 * mm});
            skCircle(sketch, "E14.6.12.0", {"center": v(338.4, -148.2) * mm, "radius": 4.5 * mm});
            skCircle(sketch, "E14.7.0.0", {"center": v(350, -287.4) * mm, "radius": 4.5 * mm});
            skCircle(sketch, "E14.7.1.0", {"center": v(350, -275.8) * mm, "radius": 4.5 * mm});
            skCircle(sketch, "E14.7.2.0", {"center": v(350, -264.2) * mm, "radius": 4.5 * mm});
            skCircle(sketch, "E14.7.3.0", {"center": v(350, -252.6) * mm, "radius": 4.5 * mm});
            skCircle(sketch, "E14.7.4.0", {"center": v(350, -241) * mm, "radius": 4.5 * mm});
            skCircle(sketch, "E14.7.5.0", {"center": v(350, -229.4) * mm, "radius": 4.5 * mm});
            skCircle(sketch, "E14.7.6.0", {"center": v(350, -217.8) * mm, "radius": 4.5 * mm});
            skCircle(sketch, "E14.7.7.0", {"center": v(350, -206.2) * mm, "radius": 4.5 * mm});
            skCircle(sketch, "E14.7.8.0", {"center": v(350, -194.6) * mm, "radius": 4.5 * mm});
            skCircle(sketch, "E14.7.9.0", {"center": v(350, -183) * mm, "radius": 4.5 * mm});
            skCircle(sketch, "E14.7.10.0", {"center": v(350, -171.4) * mm, "radius": 4.5 * mm});
            skCircle(sketch, "E14.7.11.0", {"center": v(350, -159.8) * mm, "radius": 4.5 * mm});
            skCircle(sketch, "E14.7.12.0", {"center": v(350, -148.2) * mm, "radius": 4.5 * mm});
            skCircle(sketch, "E14.8.0.0", {"center": v(361.6, -287.4) * mm, "radius": 4.5 * mm});
            skCircle(sketch, "E14.8.1.0", {"center": v(361.6, -275.8) * mm, "radius": 4.5 * mm});
            skCircle(sketch, "E14.8.2.0", {"center": v(361.6, -264.2) * mm, "radius": 4.5 * mm});
            skCircle(sketch, "E14.8.3.0", {"center": v(361.6, -252.6) * mm, "radius": 4.5 * mm});
            skCircle(sketch, "E14.8.4.0", {"center": v(361.6, -241) * mm, "radius": 4.5 * mm});
            skCircle(sketch, "E14.8.5.0", {"center": v(361.6, -229.4) * mm, "radius": 4.5 * mm});
            skCircle(sketch, "E14.8.6.0", {"center": v(361.6, -217.8) * mm, "radius": 4.5 * mm});
            skCircle(sketch, "E14.8.7.0", {"center": v(361.6, -206.2) * mm, "radius": 4.5 * mm});
            skCircle(sketch, "E14.8.8.0", {"center": v(361.6, -194.6) * mm, "radius": 4.5 * mm});
            skCircle(sketch, "E14.8.9.0", {"center": v(361.6, -183) * mm, "radius": 4.5 * mm});
            skCircle(sketch, "E14.8.10.0", {"center": v(361.6, -171.4) * mm, "radius": 4.5 * mm});
            skCircle(sketch, "E14.8.11.0", {"center": v(361.6, -159.8) * mm, "radius": 4.5 * mm});
            skCircle(sketch, "E14.8.12.0", {"center": v(361.6, -148.2) * mm, "radius": 4.5 * mm});
            skCircle(sketch, "E14.9.0.0", {"center": v(373.2, -287.4) * mm, "radius": 4.5 * mm});
            skCircle(sketch, "E14.9.1.0", {"center": v(373.2, -275.8) * mm, "radius": 4.5 * mm});
            skCircle(sketch, "E14.9.2.0", {"center": v(373.2, -264.2) * mm, "radius": 4.5 * mm});
            skCircle(sketch, "E14.9.3.0", {"center": v(373.2, -252.6) * mm, "radius": 4.5 * mm});
            skCircle(sketch, "E14.9.4.0", {"center": v(373.2, -241) * mm, "radius": 4.5 * mm});
            skCircle(sketch, "E14.9.5.0", {"center": v(373.2, -229.4) * mm, "radius": 4.5 * mm});
            skCircle(sketch, "E14.9.6.0", {"center": v(373.2, -217.8) * mm, "radius": 4.5 * mm});
            skCircle(sketch, "E14.9.7.0", {"center": v(373.2, -206.2) * mm, "radius": 4.5 * mm});
            skCircle(sketch, "E14.9.8.0", {"center": v(373.2, -194.6) * mm, "radius": 4.5 * mm});
            skCircle(sketch, "E14.9.9.0", {"center": v(373.2, -183) * mm, "radius": 4.5 * mm});
            skCircle(sketch, "E14.9.10.0", {"center": v(373.2, -171.4) * mm, "radius": 4.5 * mm});
            skCircle(sketch, "E14.9.11.0", {"center": v(373.2, -159.8) * mm, "radius": 4.5 * mm});
            skCircle(sketch, "E14.9.12.0", {"center": v(373.2, -148.2) * mm, "radius": 4.5 * mm});
            skCircle(sketch, "E14.10.0.0", {"center": v(384.8, -287.4) * mm, "radius": 4.5 * mm});
            skCircle(sketch, "E14.10.1.0", {"center": v(384.8, -275.8) * mm, "radius": 4.5 * mm});
            skCircle(sketch, "E14.10.2.0", {"center": v(384.8, -264.2) * mm, "radius": 4.5 * mm});
            skCircle(sketch, "E14.10.3.0", {"center": v(384.8, -252.6) * mm, "radius": 4.5 * mm});
            skCircle(sketch, "E14.10.4.0", {"center": v(384.8, -241) * mm, "radius": 4.5 * mm});
            skCircle(sketch, "E14.10.5.0", {"center": v(384.8, -229.4) * mm, "radius": 4.5 * mm});
            skCircle(sketch, "E14.10.6.0", {"center": v(384.8, -217.8) * mm, "radius": 4.5 * mm});
            skCircle(sketch, "E14.10.7.0", {"center": v(384.8, -206.2) * mm, "radius": 4.5 * mm});
            skCircle(sketch, "E14.10.8.0", {"center": v(384.8, -194.6) * mm, "radius": 4.5 * mm});
            skCircle(sketch, "E14.10.9.0", {"center": v(384.8, -183) * mm, "radius": 4.5 * mm});
            skCircle(sketch, "E14.10.10.0", {"center": v(384.8, -171.4) * mm, "radius": 4.5 * mm});
            skCircle(sketch, "E14.10.11.0", {"center": v(384.8, -159.8) * mm, "radius": 4.5 * mm});
            skCircle(sketch, "E14.10.12.0", {"center": v(384.8, -148.2) * mm, "radius": 4.5 * mm});
            skCircle(sketch, "E14.11.0.0", {"center": v(396.4, -287.4) * mm, "radius": 4.5 * mm});
            skCircle(sketch, "E14.11.1.0", {"center": v(396.4, -275.8) * mm, "radius": 4.5 * mm});
            skCircle(sketch, "E14.11.2.0", {"center": v(396.4, -264.2) * mm, "radius": 4.5 * mm});
            skCircle(sketch, "E14.11.3.0", {"center": v(396.4, -252.6) * mm, "radius": 4.5 * mm});
            skCircle(sketch, "E14.11.4.0", {"center": v(396.4, -241) * mm, "radius": 4.5 * mm});
            skCircle(sketch, "E14.11.5.0", {"center": v(396.4, -229.4) * mm, "radius": 4.5 * mm});
            skCircle(sketch, "E14.11.6.0", {"center": v(396.4, -217.8) * mm, "radius": 4.5 * mm});
            skCircle(sketch, "E14.11.7.0", {"center": v(396.4, -206.2) * mm, "radius": 4.5 * mm});
            skCircle(sketch, "E14.11.8.0", {"center": v(396.4, -194.6) * mm, "radius": 4.5 * mm});
            skCircle(sketch, "E14.11.9.0", {"center": v(396.4, -183) * mm, "radius": 4.5 * mm});
            skCircle(sketch, "E14.11.10.0", {"center": v(396.4, -171.4) * mm, "radius": 4.5 * mm});
            skCircle(sketch, "E14.11.11.0", {"center": v(396.4, -159.8) * mm, "radius": 4.5 * mm});
            skCircle(sketch, "E14.11.12.0", {"center": v(396.4, -148.2) * mm, "radius": 4.5 * mm});
            skCircle(sketch, "E14.12.0.0", {"center": v(408, -287.4) * mm, "radius": 4.5 * mm});
            skCircle(sketch, "E14.12.1.0", {"center": v(408, -275.8) * mm, "radius": 4.5 * mm});
            skCircle(sketch, "E14.12.2.0", {"center": v(408, -264.2) * mm, "radius": 4.5 * mm});
            skCircle(sketch, "E14.12.3.0", {"center": v(408, -252.6) * mm, "radius": 4.5 * mm});
            skCircle(sketch, "E14.12.4.0", {"center": v(408, -241) * mm, "radius": 4.5 * mm});
            skCircle(sketch, "E14.12.5.0", {"center": v(408, -229.4) * mm, "radius": 4.5 * mm});
            skCircle(sketch, "E14.12.6.0", {"center": v(408, -217.8) * mm, "radius": 4.5 * mm});
            skCircle(sketch, "E14.12.7.0", {"center": v(408, -206.2) * mm, "radius": 4.5 * mm});
            skCircle(sketch, "E14.12.8.0", {"center": v(408, -194.6) * mm, "radius": 4.5 * mm});
            skCircle(sketch, "E14.12.9.0", {"center": v(408, -183) * mm, "radius": 4.5 * mm});
            skCircle(sketch, "E14.12.10.0", {"center": v(408, -171.4) * mm, "radius": 4.5 * mm});
            skCircle(sketch, "E14.12.11.0", {"center": v(408, -159.8) * mm, "radius": 4.5 * mm});
            skCircle(sketch, "E14.12.12.0", {"center": v(408, -148.2) * mm, "radius": 4.5 * mm});
            skCircle(sketch, "E14.13.0.0", {"center": v(419.6, -287.4) * mm, "radius": 4.5 * mm});
            skCircle(sketch, "E14.13.1.0", {"center": v(419.6, -275.8) * mm, "radius": 4.5 * mm});
            skCircle(sketch, "E14.13.2.0", {"center": v(419.6, -264.2) * mm, "radius": 4.5 * mm});
            skCircle(sketch, "E14.13.3.0", {"center": v(419.6, -252.6) * mm, "radius": 4.5 * mm});
            skCircle(sketch, "E14.13.4.0", {"center": v(419.6, -241) * mm, "radius": 4.5 * mm});
            skCircle(sketch, "E14.13.5.0", {"center": v(419.6, -229.4) * mm, "radius": 4.5 * mm});
            skCircle(sketch, "E14.13.6.0", {"center": v(419.6, -217.8) * mm, "radius": 4.5 * mm});
            skCircle(sketch, "E14.13.7.0", {"center": v(419.6, -206.2) * mm, "radius": 4.5 * mm});
            skCircle(sketch, "E14.13.8.0", {"center": v(419.6, -194.6) * mm, "radius": 4.5 * mm});
            skCircle(sketch, "E14.13.9.0", {"center": v(419.6, -183) * mm, "radius": 4.5 * mm});
            skCircle(sketch, "E14.13.10.0", {"center": v(419.6, -171.4) * mm, "radius": 4.5 * mm});
            skCircle(sketch, "E14.13.11.0", {"center": v(419.6, -159.8) * mm, "radius": 4.5 * mm});
            skCircle(sketch, "E14.13.12.0", {"center": v(419.6, -148.2) * mm, "radius": 4.5 * mm});
            skCircle(sketch, "E14.14.0.0", {"center": v(431.2, -287.4) * mm, "radius": 4.5 * mm});
            skCircle(sketch, "E14.14.1.0", {"center": v(431.2, -275.8) * mm, "radius": 4.5 * mm});
            skCircle(sketch, "E14.14.2.0", {"center": v(431.2, -264.2) * mm, "radius": 4.5 * mm});
            skCircle(sketch, "E14.14.3.0", {"center": v(431.2, -252.6) * mm, "radius": 4.5 * mm});
            skCircle(sketch, "E14.14.4.0", {"center": v(431.2, -241) * mm, "radius": 4.5 * mm});
            skCircle(sketch, "E14.14.5.0", {"center": v(431.2, -229.4) * mm, "radius": 4.5 * mm});
            skCircle(sketch, "E14.14.6.0", {"center": v(431.2, -217.8) * mm, "radius": 4.5 * mm});
            skCircle(sketch, "E14.14.7.0", {"center": v(431.2, -206.2) * mm, "radius": 4.5 * mm});
            skCircle(sketch, "E14.14.8.0", {"center": v(431.2, -194.6) * mm, "radius": 4.5 * mm});
            skCircle(sketch, "E14.14.9.0", {"center": v(431.2, -183) * mm, "radius": 4.5 * mm});
            skCircle(sketch, "E14.14.10.0", {"center": v(431.2, -171.4) * mm, "radius": 4.5 * mm});
            skCircle(sketch, "E14.14.11.0", {"center": v(431.2, -159.8) * mm, "radius": 4.5 * mm});
            skCircle(sketch, "E14.14.12.0", {"center": v(431.2, -148.2) * mm, "radius": 4.5 * mm});
            skCircle(sketch, "E14.15.0.0", {"center": v(442.8, -287.4) * mm, "radius": 4.5 * mm});
            skCircle(sketch, "E14.15.1.0", {"center": v(442.8, -275.8) * mm, "radius": 4.5 * mm});
            skCircle(sketch, "E14.15.2.0", {"center": v(442.8, -264.2) * mm, "radius": 4.5 * mm});
            skCircle(sketch, "E14.15.3.0", {"center": v(442.8, -252.6) * mm, "radius": 4.5 * mm});
            skCircle(sketch, "E14.15.4.0", {"center": v(442.8, -241) * mm, "radius": 4.5 * mm});
            skCircle(sketch, "E14.15.5.0", {"center": v(442.8, -229.4) * mm, "radius": 4.5 * mm});
            skCircle(sketch, "E14.15.6.0", {"center": v(442.8, -217.8) * mm, "radius": 4.5 * mm});
            skCircle(sketch, "E14.15.7.0", {"center": v(442.8, -206.2) * mm, "radius": 4.5 * mm});
            skCircle(sketch, "E14.15.8.0", {"center": v(442.8, -194.6) * mm, "radius": 4.5 * mm});
            skCircle(sketch, "E14.15.9.0", {"center": v(442.8, -183) * mm, "radius": 4.5 * mm});
            skCircle(sketch, "E14.15.10.0", {"center": v(442.8, -171.4) * mm, "radius": 4.5 * mm});
            skCircle(sketch, "E14.15.11.0", {"center": v(442.8, -159.8) * mm, "radius": 4.5 * mm});
            skCircle(sketch, "E14.15.12.0", {"center": v(442.8, -148.2) * mm, "radius": 4.5 * mm});
            skCircle(sketch, "E14.16.0.0", {"center": v(454.4, -287.4) * mm, "radius": 4.5 * mm});
            skCircle(sketch, "E14.16.1.0", {"center": v(454.4, -275.8) * mm, "radius": 4.5 * mm});
            skCircle(sketch, "E14.16.2.0", {"center": v(454.4, -264.2) * mm, "radius": 4.5 * mm});
            skCircle(sketch, "E14.16.3.0", {"center": v(454.4, -252.6) * mm, "radius": 4.5 * mm});
            skCircle(sketch, "E14.16.4.0", {"center": v(454.4, -241) * mm, "radius": 4.5 * mm});
            skCircle(sketch, "E14.16.5.0", {"center": v(454.4, -229.4) * mm, "radius": 4.5 * mm});
            skCircle(sketch, "E14.16.6.0", {"center": v(454.4, -217.8) * mm, "radius": 4.5 * mm});
            skCircle(sketch, "E14.16.7.0", {"center": v(454.4, -206.2) * mm, "radius": 4.5 * mm});
            skCircle(sketch, "E14.16.8.0", {"center": v(454.4, -194.6) * mm, "radius": 4.5 * mm});
            skCircle(sketch, "E14.16.9.0", {"center": v(454.4, -183) * mm, "radius": 4.5 * mm});
            skCircle(sketch, "E14.16.10.0", {"center": v(454.4, -171.4) * mm, "radius": 4.5 * mm});
            skCircle(sketch, "E14.16.11.0", {"center": v(454.4, -159.8) * mm, "radius": 4.5 * mm});
            skCircle(sketch, "E14.16.12.0", {"center": v(454.4, -148.2) * mm, "radius": 4.5 * mm});
            skCircle(sketch, "E14.17.0.0", {"center": v(466, -287.4) * mm, "radius": 4.5 * mm});
            skCircle(sketch, "E14.17.1.0", {"center": v(466, -275.8) * mm, "radius": 4.5 * mm});
            skCircle(sketch, "E14.17.2.0", {"center": v(466, -264.2) * mm, "radius": 4.5 * mm});
            skCircle(sketch, "E14.17.3.0", {"center": v(466, -252.6) * mm, "radius": 4.5 * mm});
            skCircle(sketch, "E14.17.4.0", {"center": v(466, -241) * mm, "radius": 4.5 * mm});
            skCircle(sketch, "E14.17.5.0", {"center": v(466, -229.4) * mm, "radius": 4.5 * mm});
            skCircle(sketch, "E14.17.6.0", {"center": v(466, -217.8) * mm, "radius": 4.5 * mm});
            skCircle(sketch, "E14.17.7.0", {"center": v(466, -206.2) * mm, "radius": 4.5 * mm});
            skCircle(sketch, "E14.17.8.0", {"center": v(466, -194.6) * mm, "radius": 4.5 * mm});
            skCircle(sketch, "E14.17.9.0", {"center": v(466, -183) * mm, "radius": 4.5 * mm});
            skCircle(sketch, "E14.17.10.0", {"center": v(466, -171.4) * mm, "radius": 4.5 * mm});
            skCircle(sketch, "E14.17.11.0", {"center": v(466, -159.8) * mm, "radius": 4.5 * mm});
            skCircle(sketch, "E14.17.12.0", {"center": v(466, -148.2) * mm, "radius": 4.5 * mm});
            skCircle(sketch, "E14.18.0.0", {"center": v(477.6, -287.4) * mm, "radius": 4.5 * mm});
            skCircle(sketch, "E14.18.1.0", {"center": v(477.6, -275.8) * mm, "radius": 4.5 * mm});
            skCircle(sketch, "E14.18.2.0", {"center": v(477.6, -264.2) * mm, "radius": 4.5 * mm});
            skCircle(sketch, "E14.18.3.0", {"center": v(477.6, -252.6) * mm, "radius": 4.5 * mm});
            skCircle(sketch, "E14.18.4.0", {"center": v(477.6, -241) * mm, "radius": 4.5 * mm});
            skCircle(sketch, "E14.18.5.0", {"center": v(477.6, -229.4) * mm, "radius": 4.5 * mm});
            skCircle(sketch, "E14.18.6.0", {"center": v(477.6, -217.8) * mm, "radius": 4.5 * mm});
            skCircle(sketch, "E14.18.7.0", {"center": v(477.6, -206.2) * mm, "radius": 4.5 * mm});
            skCircle(sketch, "E14.18.8.0", {"center": v(477.6, -194.6) * mm, "radius": 4.5 * mm});
            skCircle(sketch, "E14.18.9.0", {"center": v(477.6, -183) * mm, "radius": 4.5 * mm});
            skCircle(sketch, "E14.18.10.0", {"center": v(477.6, -171.4) * mm, "radius": 4.5 * mm});
            skCircle(sketch, "E14.18.11.0", {"center": v(477.6, -159.8) * mm, "radius": 4.5 * mm});
            skCircle(sketch, "E14.18.12.0", {"center": v(477.6, -148.2) * mm, "radius": 4.5 * mm});
            skCircle(sketch, "E14.19.0.0", {"center": v(489.2, -287.4) * mm, "radius": 4.5 * mm});
            skCircle(sketch, "E14.19.1.0", {"center": v(489.2, -275.8) * mm, "radius": 4.5 * mm});
            skCircle(sketch, "E14.19.2.0", {"center": v(489.2, -264.2) * mm, "radius": 4.5 * mm});
            skCircle(sketch, "E14.19.3.0", {"center": v(489.2, -252.6) * mm, "radius": 4.5 * mm});
            skCircle(sketch, "E14.19.4.0", {"center": v(489.2, -241) * mm, "radius": 4.5 * mm});
            skCircle(sketch, "E14.19.5.0", {"center": v(489.2, -229.4) * mm, "radius": 4.5 * mm});
            skCircle(sketch, "E14.19.6.0", {"center": v(489.2, -217.8) * mm, "radius": 4.5 * mm});
            skCircle(sketch, "E14.19.7.0", {"center": v(489.2, -206.2) * mm, "radius": 4.5 * mm});
            skCircle(sketch, "E14.19.8.0", {"center": v(489.2, -194.6) * mm, "radius": 4.5 * mm});
            skCircle(sketch, "E14.19.9.0", {"center": v(489.2, -183) * mm, "radius": 4.5 * mm});
            skCircle(sketch, "E14.19.10.0", {"center": v(489.2, -171.4) * mm, "radius": 4.5 * mm});
            skCircle(sketch, "E14.19.11.0", {"center": v(489.2, -159.8) * mm, "radius": 4.5 * mm});
            skCircle(sketch, "E14.19.12.0", {"center": v(489.2, -148.2) * mm, "radius": 4.5 * mm});
            skCircle(sketch, "E14.20.0.0", {"center": v(500.8, -287.4) * mm, "radius": 4.5 * mm});
            skCircle(sketch, "E14.20.1.0", {"center": v(500.8, -275.8) * mm, "radius": 4.5 * mm});
            skCircle(sketch, "E14.20.2.0", {"center": v(500.8, -264.2) * mm, "radius": 4.5 * mm});
            skCircle(sketch, "E14.20.3.0", {"center": v(500.8, -252.6) * mm, "radius": 4.5 * mm});
            skCircle(sketch, "E14.20.4.0", {"center": v(500.8, -241) * mm, "radius": 4.5 * mm});
            skCircle(sketch, "E14.20.5.0", {"center": v(500.8, -229.4) * mm, "radius": 4.5 * mm});
            skCircle(sketch, "E14.20.6.0", {"center": v(500.8, -217.8) * mm, "radius": 4.5 * mm});
            skCircle(sketch, "E14.20.7.0", {"center": v(500.8, -206.2) * mm, "radius": 4.5 * mm});
            skCircle(sketch, "E14.20.8.0", {"center": v(500.8, -194.6) * mm, "radius": 4.5 * mm});
            skCircle(sketch, "E14.20.9.0", {"center": v(500.8, -183) * mm, "radius": 4.5 * mm});
            skCircle(sketch, "E14.20.10.0", {"center": v(500.8, -171.4) * mm, "radius": 4.5 * mm});
            skCircle(sketch, "E14.20.11.0", {"center": v(500.8, -159.8) * mm, "radius": 4.5 * mm});
            skCircle(sketch, "E14.20.12.0", {"center": v(500.8, -148.2) * mm, "radius": 4.5 * mm});
            skCircle(sketch, "E14.21.0.0", {"center": v(512.4, -287.4) * mm, "radius": 4.5 * mm});
            skCircle(sketch, "E14.21.1.0", {"center": v(512.4, -275.8) * mm, "radius": 4.5 * mm});
            skCircle(sketch, "E14.21.2.0", {"center": v(512.4, -264.2) * mm, "radius": 4.5 * mm});
            skCircle(sketch, "E14.21.3.0", {"center": v(512.4, -252.6) * mm, "radius": 4.5 * mm});
            skCircle(sketch, "E14.21.4.0", {"center": v(512.4, -241) * mm, "radius": 4.5 * mm});
            skCircle(sketch, "E14.21.5.0", {"center": v(512.4, -229.4) * mm, "radius": 4.5 * mm});
            skCircle(sketch, "E14.21.6.0", {"center": v(512.4, -217.8) * mm, "radius": 4.5 * mm});
            skCircle(sketch, "E14.21.7.0", {"center": v(512.4, -206.2) * mm, "radius": 4.5 * mm});
            skCircle(sketch, "E14.21.8.0", {"center": v(512.4, -194.6) * mm, "radius": 4.5 * mm});
            skCircle(sketch, "E14.21.9.0", {"center": v(512.4, -183) * mm, "radius": 4.5 * mm});
            skCircle(sketch, "E14.21.10.0", {"center": v(512.4, -171.4) * mm, "radius": 4.5 * mm});
            skCircle(sketch, "E14.21.11.0", {"center": v(512.4, -159.8) * mm, "radius": 4.5 * mm});
            skCircle(sketch, "E14.21.12.0", {"center": v(512.4, -148.2) * mm, "radius": 4.5 * mm});
            skCircle(sketch, "E14.22.0.0", {"center": v(524, -287.4) * mm, "radius": 4.5 * mm});
            skCircle(sketch, "E14.22.1.0", {"center": v(524, -275.8) * mm, "radius": 4.5 * mm});
            skCircle(sketch, "E14.22.2.0", {"center": v(524, -264.2) * mm, "radius": 4.5 * mm});
            skCircle(sketch, "E14.22.3.0", {"center": v(524, -252.6) * mm, "radius": 4.5 * mm});
            skCircle(sketch, "E14.22.4.0", {"center": v(524, -241) * mm, "radius": 4.5 * mm});
            skCircle(sketch, "E14.22.5.0", {"center": v(524, -229.4) * mm, "radius": 4.5 * mm});
            skCircle(sketch, "E14.22.6.0", {"center": v(524, -217.8) * mm, "radius": 4.5 * mm});
            skCircle(sketch, "E14.22.7.0", {"center": v(524, -206.2) * mm, "radius": 4.5 * mm});
            skCircle(sketch, "E14.22.8.0", {"center": v(524, -194.6) * mm, "radius": 4.5 * mm});
            skCircle(sketch, "E14.22.9.0", {"center": v(524, -183) * mm, "radius": 4.5 * mm});
            skCircle(sketch, "E14.22.10.0", {"center": v(524, -171.4) * mm, "radius": 4.5 * mm});
            skCircle(sketch, "E14.22.11.0", {"center": v(524, -159.8) * mm, "radius": 4.5 * mm});
            skCircle(sketch, "E14.22.12.0", {"center": v(524, -148.2) * mm, "radius": 4.5 * mm});
            skCircle(sketch, "E14.23.0.0", {"center": v(535.6, -287.4) * mm, "radius": 4.5 * mm});
            skCircle(sketch, "E14.23.1.0", {"center": v(535.6, -275.8) * mm, "radius": 4.5 * mm});
            skCircle(sketch, "E14.23.2.0", {"center": v(535.6, -264.2) * mm, "radius": 4.5 * mm});
            skCircle(sketch, "E14.23.3.0", {"center": v(535.6, -252.6) * mm, "radius": 4.5 * mm});
            skCircle(sketch, "E14.23.4.0", {"center": v(535.6, -241) * mm, "radius": 4.5 * mm});
            skCircle(sketch, "E14.23.5.0", {"center": v(535.6, -229.4) * mm, "radius": 4.5 * mm});
            skCircle(sketch, "E14.23.6.0", {"center": v(535.6, -217.8) * mm, "radius": 4.5 * mm});
            skCircle(sketch, "E14.23.7.0", {"center": v(535.6, -206.2) * mm, "radius": 4.5 * mm});
            skCircle(sketch, "E14.23.8.0", {"center": v(535.6, -194.6) * mm, "radius": 4.5 * mm});
            skCircle(sketch, "E14.23.9.0", {"center": v(535.6, -183) * mm, "radius": 4.5 * mm});
            skCircle(sketch, "E14.23.10.0", {"center": v(535.6, -171.4) * mm, "radius": 4.5 * mm});
            skCircle(sketch, "E14.23.11.0", {"center": v(535.6, -159.8) * mm, "radius": 4.5 * mm});
            skCircle(sketch, "E14.23.12.0", {"center": v(535.6, -148.2) * mm, "radius": 4.5 * mm});
            skCircle(sketch, "E14.24.0.0", {"center": v(547.2, -287.4) * mm, "radius": 4.5 * mm});
            skCircle(sketch, "E14.24.1.0", {"center": v(547.2, -275.8) * mm, "radius": 4.5 * mm});
            skCircle(sketch, "E14.24.2.0", {"center": v(547.2, -264.2) * mm, "radius": 4.5 * mm});
            skCircle(sketch, "E14.24.3.0", {"center": v(547.2, -252.6) * mm, "radius": 4.5 * mm});
            skCircle(sketch, "E14.24.4.0", {"center": v(547.2, -241) * mm, "radius": 4.5 * mm});
            skCircle(sketch, "E14.24.5.0", {"center": v(547.2, -229.4) * mm, "radius": 4.5 * mm});
            skCircle(sketch, "E14.24.6.0", {"center": v(547.2, -217.8) * mm, "radius": 4.5 * mm});
            skCircle(sketch, "E14.24.7.0", {"center": v(547.2, -206.2) * mm, "radius": 4.5 * mm});
            skCircle(sketch, "E14.24.8.0", {"center": v(547.2, -194.6) * mm, "radius": 4.5 * mm});
            skCircle(sketch, "E14.24.9.0", {"center": v(547.2, -183) * mm, "radius": 4.5 * mm});
            skCircle(sketch, "E14.24.10.0", {"center": v(547.2, -171.4) * mm, "radius": 4.5 * mm});
            skCircle(sketch, "E14.24.11.0", {"center": v(547.2, -159.8) * mm, "radius": 4.5 * mm});
            skCircle(sketch, "E14.24.12.0", {"center": v(547.2, -148.2) * mm, "radius": 4.5 * mm});
            skCircle(sketch, "E14.25.0.0", {"center": v(558.8, -287.4) * mm, "radius": 4.5 * mm});
            skCircle(sketch, "E14.25.1.0", {"center": v(558.8, -275.8) * mm, "radius": 4.5 * mm});
            skCircle(sketch, "E14.25.2.0", {"center": v(558.8, -264.2) * mm, "radius": 4.5 * mm});
            skCircle(sketch, "E14.25.3.0", {"center": v(558.8, -252.6) * mm, "radius": 4.5 * mm});
            skCircle(sketch, "E14.25.4.0", {"center": v(558.8, -241) * mm, "radius": 4.5 * mm});
            skCircle(sketch, "E14.25.5.0", {"center": v(558.8, -229.4) * mm, "radius": 4.5 * mm});
            skCircle(sketch, "E14.25.6.0", {"center": v(558.8, -217.8) * mm, "radius": 4.5 * mm});
            skCircle(sketch, "E14.25.7.0", {"center": v(558.8, -206.2) * mm, "radius": 4.5 * mm});
            skCircle(sketch, "E14.25.8.0", {"center": v(558.8, -194.6) * mm, "radius": 4.5 * mm});
            skCircle(sketch, "E14.25.9.0", {"center": v(558.8, -183) * mm, "radius": 4.5 * mm});
            skCircle(sketch, "E14.25.10.0", {"center": v(558.8, -171.4) * mm, "radius": 4.5 * mm});
            skCircle(sketch, "E14.25.11.0", {"center": v(558.8, -159.8) * mm, "radius": 4.5 * mm});
            skCircle(sketch, "E14.25.12.0", {"center": v(558.8, -148.2) * mm, "radius": 4.5 * mm});
            skCircle(sketch, "E14.26.0.0", {"center": v(570.4, -287.4) * mm, "radius": 4.5 * mm});
            skCircle(sketch, "E14.26.1.0", {"center": v(570.4, -275.8) * mm, "radius": 4.5 * mm});
            skCircle(sketch, "E14.26.2.0", {"center": v(570.4, -264.2) * mm, "radius": 4.5 * mm});
            skCircle(sketch, "E14.26.3.0", {"center": v(570.4, -252.6) * mm, "radius": 4.5 * mm});
            skCircle(sketch, "E14.26.4.0", {"center": v(570.4, -241) * mm, "radius": 4.5 * mm});
            skCircle(sketch, "E14.26.5.0", {"center": v(570.4, -229.4) * mm, "radius": 4.5 * mm});
            skCircle(sketch, "E14.26.6.0", {"center": v(570.4, -217.8) * mm, "radius": 4.5 * mm});
            skCircle(sketch, "E14.26.7.0", {"center": v(570.4, -206.2) * mm, "radius": 4.5 * mm});
            skCircle(sketch, "E14.26.8.0", {"center": v(570.4, -194.6) * mm, "radius": 4.5 * mm});
            skCircle(sketch, "E14.26.9.0", {"center": v(570.4, -183) * mm, "radius": 4.5 * mm});
            skCircle(sketch, "E14.26.10.0", {"center": v(570.4, -171.4) * mm, "radius": 4.5 * mm});
            skCircle(sketch, "E14.26.11.0", {"center": v(570.4, -159.8) * mm, "radius": 4.5 * mm});
            skCircle(sketch, "E14.26.12.0", {"center": v(570.4, -148.2) * mm, "radius": 4.5 * mm});
            skCircle(sketch, "E14.27.0.0", {"center": v(582, -287.4) * mm, "radius": 4.5 * mm});
            skCircle(sketch, "E14.27.1.0", {"center": v(582, -275.8) * mm, "radius": 4.5 * mm});
            skCircle(sketch, "E14.27.2.0", {"center": v(582, -264.2) * mm, "radius": 4.5 * mm});
            skCircle(sketch, "E14.27.3.0", {"center": v(582, -252.6) * mm, "radius": 4.5 * mm});
            skCircle(sketch, "E14.27.4.0", {"center": v(582, -241) * mm, "radius": 4.5 * mm});
            skCircle(sketch, "E14.27.5.0", {"center": v(582, -229.4) * mm, "radius": 4.5 * mm});
            skCircle(sketch, "E14.27.6.0", {"center": v(582, -217.8) * mm, "radius": 4.5 * mm});
            skCircle(sketch, "E14.27.7.0", {"center": v(582, -206.2) * mm, "radius": 4.5 * mm});
            skCircle(sketch, "E14.27.8.0", {"center": v(582, -194.6) * mm, "radius": 4.5 * mm});
            skCircle(sketch, "E14.27.9.0", {"center": v(582, -183) * mm, "radius": 4.5 * mm});
            skCircle(sketch, "E14.27.10.0", {"center": v(582, -171.4) * mm, "radius": 4.5 * mm});
            skCircle(sketch, "E14.27.11.0", {"center": v(582, -159.8) * mm, "radius": 4.5 * mm});
            skCircle(sketch, "E14.27.12.0", {"center": v(582, -148.2) * mm, "radius": 4.5 * mm});
            skCircle(sketch, "E14.28.0.0", {"center": v(593.6, -287.4) * mm, "radius": 4.5 * mm});
            skCircle(sketch, "E14.28.1.0", {"center": v(593.6, -275.8) * mm, "radius": 4.5 * mm});
            skCircle(sketch, "E14.28.2.0", {"center": v(593.6, -264.2) * mm, "radius": 4.5 * mm});
            skCircle(sketch, "E14.28.3.0", {"center": v(593.6, -252.6) * mm, "radius": 4.5 * mm});
            skCircle(sketch, "E14.28.4.0", {"center": v(593.6, -241) * mm, "radius": 4.5 * mm});
            skCircle(sketch, "E14.28.5.0", {"center": v(593.6, -229.4) * mm, "radius": 4.5 * mm});
            skCircle(sketch, "E14.28.6.0", {"center": v(593.6, -217.8) * mm, "radius": 4.5 * mm});
            skCircle(sketch, "E14.28.7.0", {"center": v(593.6, -206.2) * mm, "radius": 4.5 * mm});
            skCircle(sketch, "E14.28.8.0", {"center": v(593.6, -194.6) * mm, "radius": 4.5 * mm});
            skCircle(sketch, "E14.28.9.0", {"center": v(593.6, -183) * mm, "radius": 4.5 * mm});
            skCircle(sketch, "E14.28.10.0", {"center": v(593.6, -171.4) * mm, "radius": 4.5 * mm});
            skCircle(sketch, "E14.28.11.0", {"center": v(593.6, -159.8) * mm, "radius": 4.5 * mm});
            skCircle(sketch, "E14.28.12.0", {"center": v(593.6, -148.2) * mm, "radius": 4.5 * mm});
            skCircle(sketch, "E14.29.0.0", {"center": v(605.2, -287.4) * mm, "radius": 4.5 * mm});
            skCircle(sketch, "E14.29.1.0", {"center": v(605.2, -275.8) * mm, "radius": 4.5 * mm});
            skCircle(sketch, "E14.29.2.0", {"center": v(605.2, -264.2) * mm, "radius": 4.5 * mm});
            skCircle(sketch, "E14.29.3.0", {"center": v(605.2, -252.6) * mm, "radius": 4.5 * mm});
            skCircle(sketch, "E14.29.4.0", {"center": v(605.2, -241) * mm, "radius": 4.5 * mm});
            skCircle(sketch, "E14.29.5.0", {"center": v(605.2, -229.4) * mm, "radius": 4.5 * mm});
            skCircle(sketch, "E14.29.6.0", {"center": v(605.2, -217.8) * mm, "radius": 4.5 * mm});
            skCircle(sketch, "E14.29.7.0", {"center": v(605.2, -206.2) * mm, "radius": 4.5 * mm});
            skCircle(sketch, "E14.29.8.0", {"center": v(605.2, -194.6) * mm, "radius": 4.5 * mm});
            skCircle(sketch, "E14.29.9.0", {"center": v(605.2, -183) * mm, "radius": 4.5 * mm});
            skCircle(sketch, "E14.29.10.0", {"center": v(605.2, -171.4) * mm, "radius": 4.5 * mm});
            skCircle(sketch, "E14.29.11.0", {"center": v(605.2, -159.8) * mm, "radius": 4.5 * mm});
            skCircle(sketch, "E14.29.12.0", {"center": v(605.2, -148.2) * mm, "radius": 4.5 * mm});
            skLineSegment(sketch, "E14.direction1", {"start": v(268.8, -287.4) * mm, "end": v(280.4, -287.4) * mm, "construction": true});
            skLineSegment(sketch, "E14.direction2", {"start": v(268.8, -287.4) * mm, "end": v(268.8, -275.8) * mm, "construction": true});
            skSolve(sketch);
        }
        {
            var Q0;
            Q0 = qSketchRegion(id + "F13", true);
            extrude(context, id + "F14", {"entities" : qUnion([Q0]), "operationType" : NewBodyOperationType.REMOVE, "oppositeDirection" : true, "depth" : 25 * mm});
        }
        {
            var Q0;
            Q0=makeQuery(id+"F9.opExtrude","CAP_FACE",FACE,{"disambiguationData":[OSD([sQuery(id+"F8.wireOp",EDGE,"E10.bottom"),sQuery(id+"F8.wireOp",EDGE,"E10.top"),sQuery(id+"F8.wireOp",EDGE,"E10.left"),sQuery(id+"F8.wireOp",EDGE,"E10.right")])],"isStart":false});
            var sketch = newSketch(context, id + "F15", { "sketchPlane" : qUnion([Q0])});
            skLineSegment(sketch, "E15.bottom", {"start": v(302, -72.5) * mm, "end": v(572, -72.5) * mm});
            skLineSegment(sketch, "E15.top", {"start": v(302, -112.5) * mm, "end": v(572, -112.5) * mm});
            skLineSegment(sketch, "E15.left", {"start": v(302, -72.5) * mm, "end": v(302, -112.5) * mm});
            skLineSegment(sketch, "E15.right", {"start": v(572, -72.5) * mm, "end": v(572, -112.5) * mm});
            skArc(sketch, "E16", {"start": v(302, -112.5) * mm, "mid": v(294.36, -92.5) * mm, "end": v(302, -72.5) * mm});
            skPoint(sketch, "E16.centerSnap0", {"position": v(302, -92.5) * mm});
            skLineSegment(sketch, "E17", {"start": v(437, -72.5) * mm, "end": v(437, -112.5) * mm, "construction": true});
            skArc(sketch, "E18.MirrorCS", {"start": v(572, -112.5) * mm, "mid": v(579.64, -92.5) * mm, "end": v(572, -72.5) * mm});
            skSolve(sketch);
        }
        {
            var Q0;
            Q0 = qSketchRegion(id + "F15", true);
            extrude(context, id + "F16", {"entities" : qUnion([Q0]), "operationType" : NewBodyOperationType.REMOVE, "oppositeDirection" : true, "depth" : 1.5 * mm});
        }
        {
            var Q0;
            Q0=makeQuery(id+"F16.boolean.opBoolean","COPY",FACE,{"derivedFrom":makeQuery(id+"F16.opExtrude","CAP_FACE",FACE,{"disambiguationData":[OSD([sQuery(id+"F15.wireOp",EDGE,"E15.bottom"),sQuery(id+"F15.wireOp",EDGE,"E15.top"),sQuery(id+"F15.wireOp",EDGE,"E16"),sQuery(id+"F15.wireOp",EDGE,"E18.MirrorCS")])],"isStart":false})});
            extrude(context, id + "F17", {"entities" : qUnion([Q0]), "depth" : 1 * mm});
        }
        {
            var Q0;
            Q0=makeQuery(id+"F9.opExtrude","CAP_FACE",FACE,{"disambiguationData":[OSD([sQuery(id+"F8.wireOp",EDGE,"E10.bottom"),sQuery(id+"F8.wireOp",EDGE,"E10.top"),sQuery(id+"F8.wireOp",EDGE,"E10.left"),sQuery(id+"F8.wireOp",EDGE,"E10.right")])],"isStart":false});
            var sketch = newSketch(context, id + "F18", { "sketchPlane" : qUnion([Q0])});
            skLineSegment(sketch, "E19", {"start": v(387.19, -357.5) * mm, "end": v(501.38, -357.5) * mm, "construction": true});
            skLineSegment(sketch, "E20", {"start": v(501.74, -337.5) * mm, "end": v(388.42, -337.5) * mm, "construction": true});
            skLineSegment(sketch, "E21", {"start": v(481.95, -357.5) * mm, "end": v(493.5, -337.5) * mm});
            skLineSegment(sketch, "E22", {"start": v(493.5, -337.5) * mm, "end": v(484.17, -337.5) * mm});
            skLineSegment(sketch, "E23", {"start": v(484.17, -337.5) * mm, "end": v(473.17, -346.5) * mm});
            skLineSegment(sketch, "E24", {"start": v(473.17, -346.5) * mm, "end": v(473.17, -337.5) * mm});
            skLineSegment(sketch, "E25", {"start": v(473.17, -337.5) * mm, "end": v(464.9, -337.5) * mm});
            skLineSegment(sketch, "E26", {"start": v(464.9, -337.5) * mm, "end": v(455.09, -354.5) * mm});
            skLineSegment(sketch, "E27", {"start": v(455.09, -354.5) * mm, "end": v(450.08, -337.5) * mm});
            skLineSegment(sketch, "E28", {"start": v(450.08, -337.5) * mm, "end": v(445.08, -337.5) * mm});
            skLineSegment(sketch, "E29", {"start": v(445.08, -337.5) * mm, "end": v(435.27, -354.5) * mm});
            skLineSegment(sketch, "E30", {"start": v(435.27, -354.5) * mm, "end": v(433.27, -354.5) * mm});
            skLineSegment(sketch, "E31", {"start": v(433.27, -354.5) * mm, "end": v(431.2, -347.5) * mm});
            skLineSegment(sketch, "E32", {"start": v(431.2, -337.5) * mm, "end": v(415.64, -337.5) * mm});
            skLineSegment(sketch, "E33", {"start": v(415.64, -337.5) * mm, "end": v(405.82, -354.5) * mm});
            skLineSegment(sketch, "E34", {"start": v(405.82, -354.5) * mm, "end": v(400.05, -354.5) * mm});
            skLineSegment(sketch, "E35", {"start": v(400.05, -354.5) * mm, "end": v(408.7, -339.5) * mm});
            skLineSegment(sketch, "E36", {"start": v(408.7, -339.5) * mm, "end": v(396.32, -339.5) * mm});
            skLineSegment(sketch, "E37", {"start": v(396.32, -339.5) * mm, "end": v(394.59, -342.5) * mm});
            skLineSegment(sketch, "E38", {"start": v(394.59, -342.5) * mm, "end": v(396.59, -342.5) * mm});
            skLineSegment(sketch, "E39", {"start": v(396.59, -342.5) * mm, "end": v(389.66, -354.5) * mm});
            skLineSegment(sketch, "E40", {"start": v(389.66, -354.5) * mm, "end": v(388.18, -354.5) * mm});
            skLineSegment(sketch, "E41", {"start": v(391.6, -334.5) * mm, "end": v(411.6, -334.5) * mm});
            skLineSegment(sketch, "E42", {"start": v(411.6, -334.5) * mm, "end": v(413.9, -330.5) * mm});
            skLineSegment(sketch, "E43", {"start": v(413.9, -330.5) * mm, "end": v(391.6, -330.5) * mm});
            skLineSegment(sketch, "E44", {"start": v(386.79, -357.5) * mm, "end": v(387.93, -357.5) * mm});
            skLineSegment(sketch, "E45", {"start": v(387.93, -357.5) * mm, "end": v(382.15, -367.5) * mm});
            skLineSegment(sketch, "E46", {"start": v(382.15, -367.5) * mm, "end": v(392.54, -367.5) * mm});
            skLineSegment(sketch, "E47", {"start": v(392.54, -367.5) * mm, "end": v(398.32, -357.5) * mm});
            skLineSegment(sketch, "E48", {"start": v(398.32, -357.5) * mm, "end": v(414.48, -357.5) * mm});
            skLineSegment(sketch, "E49", {"start": v(414.48, -357.5) * mm, "end": v(420.26, -347.5) * mm});
            skLineSegment(sketch, "E50", {"start": v(421.82, -347.5) * mm, "end": v(424.77, -357.5) * mm});
            skLineSegment(sketch, "E51", {"start": v(424.77, -357.5) * mm, "end": v(437, -357.5) * mm});
            skLineSegment(sketch, "E52", {"start": v(437, -357.5) * mm, "end": v(440.46, -351.5) * mm});
            skLineSegment(sketch, "E53", {"start": v(440.46, -351.5) * mm, "end": v(444.82, -351.5) * mm});
            skLineSegment(sketch, "E54", {"start": v(444.82, -351.5) * mm, "end": v(446.59, -357.5) * mm});
            skLineSegment(sketch, "E55", {"start": v(446.59, -357.5) * mm, "end": v(456.82, -357.5) * mm});
            skLineSegment(sketch, "E56", {"start": v(456.82, -357.5) * mm, "end": v(463.17, -346.5) * mm});
            skLineSegment(sketch, "E57", {"start": v(463.17, -346.5) * mm, "end": v(464.17, -346.5) * mm});
            skLineSegment(sketch, "E58", {"start": v(464.17, -346.5) * mm, "end": v(464.17, -357.74) * mm});
            skLineSegment(sketch, "E59", {"start": v(464.17, -357.74) * mm, "end": v(477.9, -346.5) * mm});
            skLineSegment(sketch, "E60", {"start": v(477.9, -346.5) * mm, "end": v(471.56, -357.5) * mm});
            skLineSegment(sketch, "E61", {"start": v(471.56, -357.5) * mm, "end": v(481.95, -357.5) * mm});
            skLineSegment(sketch, "E62", {"start": v(442.2, -348.5) * mm, "end": v(443.94, -348.5) * mm});
            skLineSegment(sketch, "E63", {"start": v(443.94, -348.5) * mm, "end": v(443.35, -346.5) * mm});
            skLineSegment(sketch, "E64", {"start": v(443.35, -346.5) * mm, "end": v(442.2, -348.5) * mm});
            skLineSegment(sketch, "E65", {"start": v(420.26, -347.5) * mm, "end": v(423.14, -342.5) * mm});
            skLineSegment(sketch, "E66", {"start": v(423.14, -342.5) * mm, "end": v(426.14, -342.5) * mm});
            skLineSegment(sketch, "E67", {"start": v(421.82, -347.5) * mm, "end": v(422.33, -347.5) * mm});
            skPoint(sketch, "E68", {"position": v(421.3, -347.5) * mm});
            skPoint(sketch, "E69.orphan", {"position": v(421.3, -345.7) * mm});
            skLineSegment(sketch, "E70", {"start": v(422.33, -347.5) * mm, "end": v(426.14, -347.5) * mm});
            skArc(sketch, "E71", {"start": v(426.14, -347.5) * mm, "mid": v(428.64, -345) * mm, "end": v(426.14, -342.5) * mm});
            skArc(sketch, "E72", {"start": v(431.2, -347.5) * mm, "mid": v(437.23, -342.5) * mm, "end": v(431.2, -337.5) * mm});
            skArc(sketch, "E73", {"start": v(391.6, -334.5) * mm, "mid": v(381.58, -341.66) * mm, "end": v(385.13, -353.46) * mm});
            skArc(sketch, "E74", {"start": v(391.6, -330.5) * mm, "mid": v(379.1, -337.07) * mm, "end": v(377.45, -351.09) * mm});
            skPoint(sketch, "E75.visualSharp", {"position": v(386.77, -354.5) * mm});
            skArc(sketch, "E75.filletArc", {"start": v(385.13, -353.46) * mm, "mid": v(386.57, -354.23) * mm, "end": v(388.18, -354.5) * mm});
            skPoint(sketch, "E76.visualSharp", {"position": v(382.15, -357.5) * mm});
            skArc(sketch, "E76.filletArc", {"start": v(377.45, -351.09) * mm, "mid": v(381.12, -355.74) * mm, "end": v(386.79, -357.5) * mm});
            skSolve(sketch);
        }
        {
            var Q0;
            Q0 = qSketchRegion(id + "F18", true);
            extrude(context, id + "F19", {"entities" : qUnion([Q0]), "operationType" : NewBodyOperationType.REMOVE, "oppositeDirection" : true, "depth" : 1.5 * mm});
        }
        {
            var Q0;
            Q0=makeQuery(id+"F19.boolean.opBoolean","COPY",FACE,{"derivedFrom":makeQuery(id+"F19.opExtrude","CAP_FACE",FACE,{"disambiguationData":[OSD([sQuery(id+"F18.wireOp",EDGE,"E21"),sQuery(id+"F18.wireOp",EDGE,"E22"),sQuery(id+"F18.wireOp",EDGE,"E23"),sQuery(id+"F18.wireOp",EDGE,"E24"),sQuery(id+"F18.wireOp",EDGE,"E25"),sQuery(id+"F18.wireOp",EDGE,"E26"),sQuery(id+"F18.wireOp",EDGE,"E27"),sQuery(id+"F18.wireOp",EDGE,"E28"),sQuery(id+"F18.wireOp",EDGE,"E29"),sQuery(id+"F18.wireOp",EDGE,"E30"),sQuery(id+"F18.wireOp",EDGE,"E31"),sQuery(id+"F18.wireOp",EDGE,"E32"),sQuery(id+"F18.wireOp",EDGE,"E33"),sQuery(id+"F18.wireOp",EDGE,"E34"),sQuery(id+"F18.wireOp",EDGE,"E35"),sQuery(id+"F18.wireOp",EDGE,"E36"),sQuery(id+"F18.wireOp",EDGE,"E37"),sQuery(id+"F18.wireOp",EDGE,"E38"),sQuery(id+"F18.wireOp",EDGE,"E39"),sQuery(id+"F18.wireOp",EDGE,"E40"),sQuery(id+"F18.wireOp",EDGE,"E41"),sQuery(id+"F18.wireOp",EDGE,"E42"),sQuery(id+"F18.wireOp",EDGE,"E43"),sQuery(id+"F18.wireOp",EDGE,"E44"),sQuery(id+"F18.wireOp",EDGE,"E45"),sQuery(id+"F18.wireOp",EDGE,"E46"),sQuery(id+"F18.wireOp",EDGE,"E47"),sQuery(id+"F18.wireOp",EDGE,"E48"),sQuery(id+"F18.wireOp",EDGE,"E49"),sQuery(id+"F18.wireOp",EDGE,"E50"),sQuery(id+"F18.wireOp",EDGE,"E51"),sQuery(id+"F18.wireOp",EDGE,"E52"),sQuery(id+"F18.wireOp",EDGE,"E53"),sQuery(id+"F18.wireOp",EDGE,"E54"),sQuery(id+"F18.wireOp",EDGE,"E55"),sQuery(id+"F18.wireOp",EDGE,"E56"),sQuery(id+"F18.wireOp",EDGE,"E57"),sQuery(id+"F18.wireOp",EDGE,"E58"),sQuery(id+"F18.wireOp",EDGE,"E59"),sQuery(id+"F18.wireOp",EDGE,"E60"),sQuery(id+"F18.wireOp",EDGE,"E61"),sQuery(id+"F18.wireOp",EDGE,"E62"),sQuery(id+"F18.wireOp",EDGE,"E63"),sQuery(id+"F18.wireOp",EDGE,"E64"),sQuery(id+"F18.wireOp",EDGE,"E65"),sQuery(id+"F18.wireOp",EDGE,"E66"),sQuery(id+"F18.wireOp",EDGE,"E67"),sQuery(id+"F18.wireOp",EDGE,"E70"),sQuery(id+"F18.wireOp",EDGE,"E71"),sQuery(id+"F18.wireOp",EDGE,"E72"),sQuery(id+"F18.wireOp",EDGE,"E73"),sQuery(id+"F18.wireOp",EDGE,"E74"),sQuery(id+"F18.wireOp",EDGE,"E75.filletArc"),sQuery(id+"F18.wireOp",EDGE,"E76.filletArc")])],"isStart":false})});
            extrude(context, id + "F20", {"entities" : qUnion([Q0]), "depth" : 1 * mm});
        }
    });
